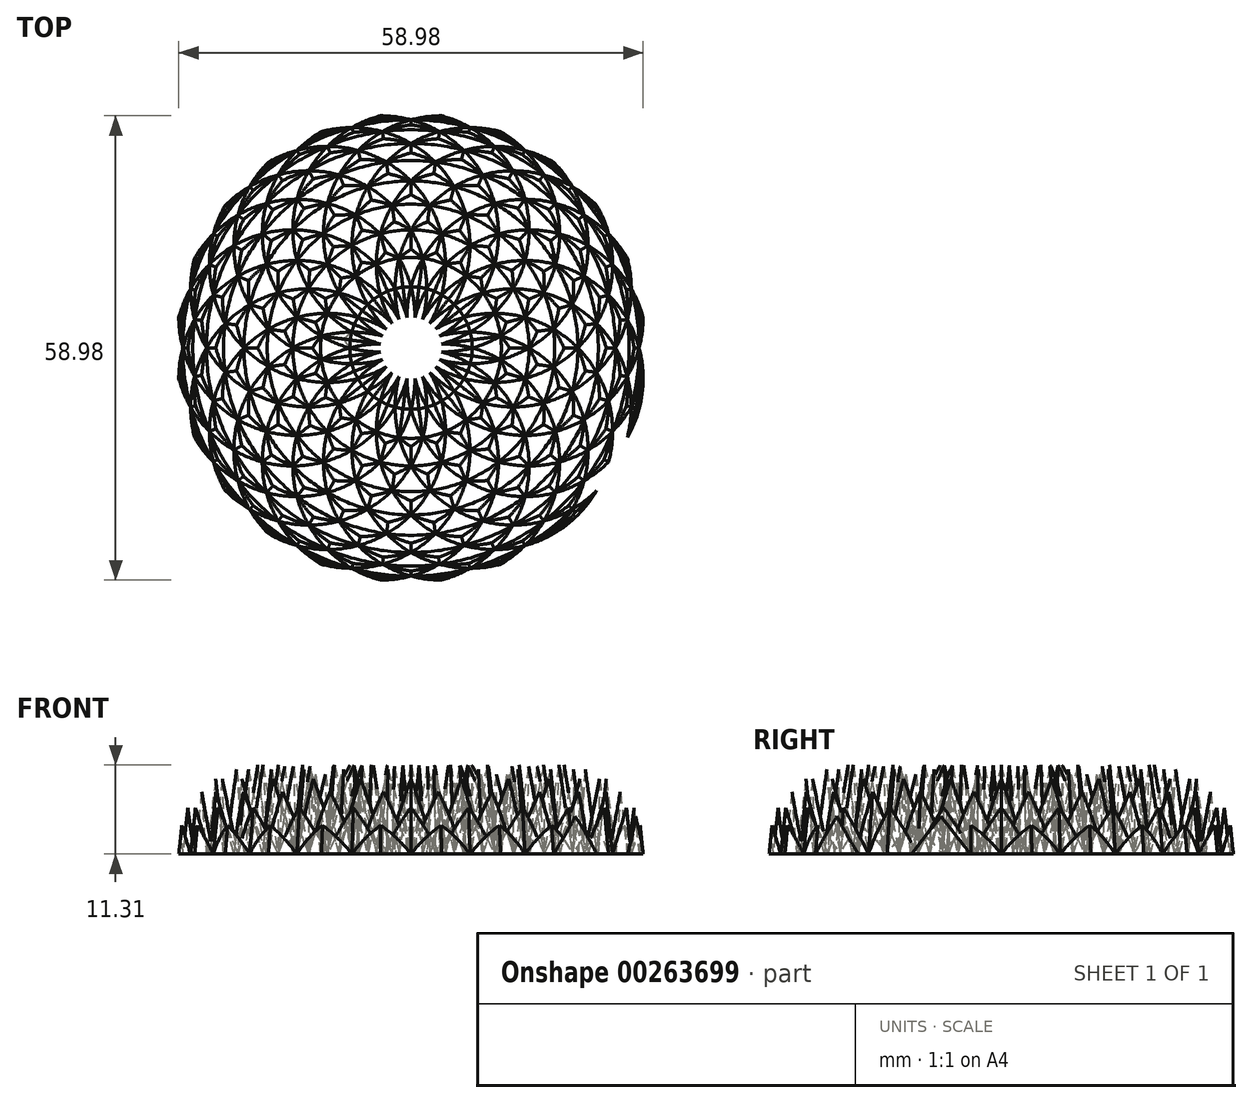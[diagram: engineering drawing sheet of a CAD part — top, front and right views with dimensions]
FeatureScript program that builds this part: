
annotation { "Feature Type Name" : "Feature", "Feature Type Description" : "" }
export const myFeature = defineFeature(function(context is Context, id is Id, definition is map)
    precondition{}
    {
        {
            var Q0;
            Q0=qCreatedBy(makeId("Top.planeOp"),FACE);
            var sketch = newSketch(context, id + "F0", { "sketchPlane" : qUnion([Q0])});
            skCircle(sketch, "E0", {"center": v(0, 0) * mm, "radius": 15 * mm});
            skLineSegment(sketch, "E1", {"start": v(-15, 0) * mm, "end": v(15, 0) * mm, "construction": true});
            skLineSegment(sketch, "E2", {"start": v(0, 15) * mm, "end": v(0, -15) * mm, "construction": true});
            skCircle(sketch, "E3", {"center": v(15, 0) * mm, "radius": 15 * mm});
            skCircle(sketch, "E4", {"center": v(7.5, 13) * mm, "radius": 15 * mm});
            skCircle(sketch, "E5", {"center": v(7.5, -13) * mm, "radius": 15 * mm});
            skCircle(sketch, "E6", {"center": v(-7.5, 13) * mm, "radius": 15 * mm});
            skCircle(sketch, "E7", {"center": v(-7.5, -13) * mm, "radius": 15 * mm});
            skCircle(sketch, "E8", {"center": v(-15, 0) * mm, "radius": 15 * mm});
            skLineSegment(sketch, "E9", {"start": v(0, 0) * mm, "end": v(22.5, 13) * mm, "construction": true});
            skCircle(sketch, "E10", {"center": v(13, 7.5) * mm, "radius": 15 * mm});
            skCircle(sketch, "E11", {"center": v(13, -7.5) * mm, "radius": 15 * mm});
            skCircle(sketch, "E12", {"center": v(0, -15) * mm, "radius": 15 * mm});
            skCircle(sketch, "E13", {"center": v(-13, -7.5) * mm, "radius": 15 * mm});
            skCircle(sketch, "E14", {"center": v(-13, 7.5) * mm, "radius": 15 * mm});
            skCircle(sketch, "E15", {"center": v(0, 15) * mm, "radius": 15 * mm});
            skLineSegment(sketch, "E16", {"start": v(7.5, 2) * mm, "end": v(20.5, 5.5) * mm, "construction": true});
            skCircle(sketch, "E17", {"center": v(14.49, 3.88) * mm, "radius": 15 * mm});
            skCircle(sketch, "E18", {"center": v(10.6, -10.6) * mm, "radius": 15 * mm});
            skCircle(sketch, "E19", {"center": v(-3.88, -14.49) * mm, "radius": 15 * mm});
            skCircle(sketch, "E20", {"center": v(-14.49, -3.88) * mm, "radius": 15 * mm});
            skCircle(sketch, "E21", {"center": v(-10.6, 10.6) * mm, "radius": 15 * mm});
            skCircle(sketch, "E22", {"center": v(3.88, 14.49) * mm, "radius": 15 * mm});
            skLineSegment(sketch, "E23", {"start": v(-2, 7.5) * mm, "end": v(-5.5, 20.5) * mm, "construction": true});
            skCircle(sketch, "E24", {"center": v(-3.88, 14.49) * mm, "radius": 15 * mm});
            skCircle(sketch, "E25", {"center": v(10.6, 10.6) * mm, "radius": 15 * mm});
            skCircle(sketch, "E26", {"center": v(14.49, -3.88) * mm, "radius": 15 * mm});
            skCircle(sketch, "E27", {"center": v(3.88, -14.49) * mm, "radius": 15 * mm});
            skCircle(sketch, "E28", {"center": v(-10.6, -10.6) * mm, "radius": 15 * mm});
            skCircle(sketch, "E29", {"center": v(-14.49, 3.88) * mm, "radius": 15 * mm});
            skCircle(sketch, "E30", {"center": v(0, 0) * mm, "radius": 18.26 * mm});
            skLineSegment(sketch, "E31", {"start": v(-6.99, 16.87) * mm, "end": v(-2.38, 18.1) * mm, "construction": true});
            skCircle(sketch, "E32", {"center": v(0, 0) * mm, "radius": 21.21 * mm});
            skLineSegment(sketch, "E33", {"start": v(0, 0) * mm, "end": v(7.5, 28) * mm, "construction": true});
            skCircle(sketch, "E34", {"center": v(0, 0) * mm, "radius": 28.98 * mm});
            skLineSegment(sketch, "E35", {"start": v(0, 0) * mm, "end": v(3.1, 23.6) * mm, "construction": true});
            skCircle(sketch, "E36", {"center": v(0, 0) * mm, "radius": 23.8 * mm});
            skLineSegment(sketch, "E37", {"start": v(0, 0) * mm, "end": v(-3.62, 27.48) * mm, "construction": true});
            skCircle(sketch, "E38", {"center": v(0, 0) * mm, "radius": 27.72 * mm});
            skLineSegment(sketch, "E39", {"start": v(0, 0) * mm, "end": v(-13, 22.5) * mm, "construction": true});
            skCircle(sketch, "E40", {"center": v(0, 0) * mm, "radius": 25.98 * mm});
            skLineSegment(sketch, "E41", {"start": v(0, 0) * mm, "end": v(-9.1, 6.99) * mm, "construction": true});
            skCircle(sketch, "E42", {"center": v(0, 0) * mm, "radius": 11.48 * mm});
            skLineSegment(sketch, "E43", {"start": v(0, 0) * mm, "end": v(-6.72, 3.88) * mm, "construction": true});
            skCircle(sketch, "E44", {"center": v(0, 0) * mm, "radius": 7.76 * mm});
            skLineSegment(sketch, "E45", {"start": v(0, 0) * mm, "end": v(-2.38, -3.1) * mm, "construction": true});
            skCircle(sketch, "E46", {"center": v(0, 0) * mm, "radius": 3.92 * mm});
            skCircle(sketch, "E47", {"center": v(0, 0) * mm, "radius": 30 * mm});
            skSolve(sketch);
        }
        {
            var Q0;
            {var subQ0=sQuery(id+"F0.wireOp",EDGE,"E44");var subQ1=sQuery(id+"F0.wireOp",EDGE,"E3");var subQ2=makeQuery(id+"F0.imprint","INTERSECT",VERTEX,{"derivedFrom":[subQ1,sQuery(id+"F0.wireOp",EDGE,"E14"),subQ0]});Q0=makeQuery(id+"F0.imprint","IMPRINT",FACE,{"disambiguationData":[TD([[makeQuery(id+"F0.imprint","IMPRINT",EDGE,{"disambiguationData":[TD([[subQ2,-1.0]])],"derivedFrom":subQ1}),-1.0]])]});}
            var Q1;
            {var subQ0=sQuery(id+"F0.wireOp",EDGE,"E44");var subQ1=sQuery(id+"F0.wireOp",EDGE,"E14");var subQ2=makeQuery(id+"F0.imprint","INTERSECT",VERTEX,{"derivedFrom":[sQuery(id+"F0.wireOp",EDGE,"E3"),subQ1,subQ0]});Q1=makeQuery(id+"F0.imprint","IMPRINT",FACE,{"disambiguationData":[TD([[makeQuery(id+"F0.imprint","IMPRINT",EDGE,{"disambiguationData":[TD([[subQ2,-1.0]])],"derivedFrom":subQ1}),1.0]])]});}
            var Q2;
            {var subQ0=sQuery(id+"F0.wireOp",EDGE,"E44");var subQ1=sQuery(id+"F0.wireOp",EDGE,"E14");var subQ2=makeQuery(id+"F0.imprint","INTERSECT",VERTEX,{"derivedFrom":[sQuery(id+"F0.wireOp",EDGE,"E3"),subQ1,subQ0]});Q2=makeQuery(id+"F0.imprint","IMPRINT",FACE,{"disambiguationData":[TD([[makeQuery(id+"F0.imprint","IMPRINT",EDGE,{"disambiguationData":[TD([[subQ2,1.0]])],"derivedFrom":subQ1}),-1.0]])]});}
            var Q3;
            {var subQ0=sQuery(id+"F0.wireOp",EDGE,"E21");var subQ1=sQuery(id+"F0.wireOp",EDGE,"E3");var subQ2=makeQuery(id+"F0.imprint","INTERSECT",VERTEX,{"derivedFrom":[subQ1,subQ0,sQuery(id+"F0.wireOp",EDGE,"E42")]});Q3=makeQuery(id+"F0.imprint","IMPRINT",FACE,{"disambiguationData":[TD([[makeQuery(id+"F0.imprint","IMPRINT",EDGE,{"disambiguationData":[TD([[subQ2,-1.0]])],"derivedFrom":subQ1}),1.0]])]});}
            var Q4;
            {var subQ0=sQuery(id+"F0.wireOp",EDGE,"E44");var subQ1=sQuery(id+"F0.wireOp",EDGE,"E11");var subQ2=makeQuery(id+"F0.imprint","INTERSECT",VERTEX,{"derivedFrom":[sQuery(id+"F0.wireOp",EDGE,"E6"),subQ1,subQ0]});Q4=makeQuery(id+"F0.imprint","IMPRINT",FACE,{"disambiguationData":[TD([[makeQuery(id+"F0.imprint","IMPRINT",EDGE,{"disambiguationData":[TD([[subQ2,-1.0]])],"derivedFrom":subQ1}),-1.0]])]});}
            var Q5;
            {var subQ0=sQuery(id+"F0.wireOp",EDGE,"E44");var subQ1=sQuery(id+"F0.wireOp",EDGE,"E6");var subQ2=makeQuery(id+"F0.imprint","INTERSECT",VERTEX,{"derivedFrom":[subQ1,sQuery(id+"F0.wireOp",EDGE,"E11"),subQ0]});Q5=makeQuery(id+"F0.imprint","IMPRINT",FACE,{"disambiguationData":[TD([[makeQuery(id+"F0.imprint","IMPRINT",EDGE,{"disambiguationData":[TD([[subQ2,-1.0]])],"derivedFrom":subQ1}),1.0]])]});}
            var Q6;
            {var subQ0=sQuery(id+"F0.wireOp",EDGE,"E18");var subQ1=sQuery(id+"F0.wireOp",EDGE,"E6");var subQ2=makeQuery(id+"F0.imprint","INTERSECT",VERTEX,{"derivedFrom":[subQ1,subQ0,sQuery(id+"F0.wireOp",EDGE,"E46")]});Q6=makeQuery(id+"F0.imprint","IMPRINT",FACE,{"disambiguationData":[TD([[makeQuery(id+"F0.imprint","IMPRINT",EDGE,{"disambiguationData":[TD([[subQ2,-1.0]])],"derivedFrom":subQ1}),-1.0]])]});}
            var Q7;
            {var subQ0=sQuery(id+"F0.wireOp",EDGE,"E44");var subQ1=sQuery(id+"F0.wireOp",EDGE,"E11");var subQ2=makeQuery(id+"F0.imprint","INTERSECT",VERTEX,{"derivedFrom":[sQuery(id+"F0.wireOp",EDGE,"E6"),subQ1,subQ0]});Q7=makeQuery(id+"F0.imprint","IMPRINT",FACE,{"disambiguationData":[TD([[makeQuery(id+"F0.imprint","IMPRINT",EDGE,{"disambiguationData":[TD([[subQ2,1.0]])],"derivedFrom":subQ1}),1.0]])]});}
            var Q8;
            {var subQ0=sQuery(id+"F0.wireOp",EDGE,"E44");var subQ1=sQuery(id+"F0.wireOp",EDGE,"E5");var subQ2=makeQuery(id+"F0.imprint","INTERSECT",VERTEX,{"derivedFrom":[subQ1,sQuery(id+"F0.wireOp",EDGE,"E15"),subQ0]});Q8=makeQuery(id+"F0.imprint","IMPRINT",FACE,{"disambiguationData":[TD([[makeQuery(id+"F0.imprint","IMPRINT",EDGE,{"disambiguationData":[TD([[subQ2,-1.0]])],"derivedFrom":subQ1}),-1.0]])]});}
            var Q9;
            {var subQ0=sQuery(id+"F0.wireOp",EDGE,"E44");var subQ1=sQuery(id+"F0.wireOp",EDGE,"E15");var subQ2=makeQuery(id+"F0.imprint","INTERSECT",VERTEX,{"derivedFrom":[sQuery(id+"F0.wireOp",EDGE,"E5"),subQ1,subQ0]});Q9=makeQuery(id+"F0.imprint","IMPRINT",FACE,{"disambiguationData":[TD([[makeQuery(id+"F0.imprint","IMPRINT",EDGE,{"disambiguationData":[TD([[subQ2,-1.0]])],"derivedFrom":subQ1}),1.0]])]});}
            var Q10;
            {var subQ0=sQuery(id+"F0.wireOp",EDGE,"E44");var subQ1=sQuery(id+"F0.wireOp",EDGE,"E15");var subQ2=makeQuery(id+"F0.imprint","INTERSECT",VERTEX,{"derivedFrom":[sQuery(id+"F0.wireOp",EDGE,"E5"),subQ1,subQ0]});Q10=makeQuery(id+"F0.imprint","IMPRINT",FACE,{"disambiguationData":[TD([[makeQuery(id+"F0.imprint","IMPRINT",EDGE,{"disambiguationData":[TD([[subQ2,1.0]])],"derivedFrom":subQ1}),-1.0]])]});}
            var Q11;
            {var subQ0=sQuery(id+"F0.wireOp",EDGE,"E22");var subQ1=sQuery(id+"F0.wireOp",EDGE,"E5");var subQ2=makeQuery(id+"F0.imprint","INTERSECT",VERTEX,{"derivedFrom":[subQ1,subQ0,sQuery(id+"F0.wireOp",EDGE,"E42")]});Q11=makeQuery(id+"F0.imprint","IMPRINT",FACE,{"disambiguationData":[TD([[makeQuery(id+"F0.imprint","IMPRINT",EDGE,{"disambiguationData":[TD([[subQ2,-1.0]])],"derivedFrom":subQ1}),1.0]])]});}
            var Q12;
            {var subQ0=sQuery(id+"F0.wireOp",EDGE,"E44");var subQ1=sQuery(id+"F0.wireOp",EDGE,"E12");var subQ2=makeQuery(id+"F0.imprint","INTERSECT",VERTEX,{"derivedFrom":[sQuery(id+"F0.wireOp",EDGE,"E4"),subQ1,subQ0]});Q12=makeQuery(id+"F0.imprint","IMPRINT",FACE,{"disambiguationData":[TD([[makeQuery(id+"F0.imprint","IMPRINT",EDGE,{"disambiguationData":[TD([[subQ2,-1.0]])],"derivedFrom":subQ1}),-1.0]])]});}
            var Q13;
            {var subQ0=sQuery(id+"F0.wireOp",EDGE,"E44");var subQ1=sQuery(id+"F0.wireOp",EDGE,"E4");var subQ2=makeQuery(id+"F0.imprint","INTERSECT",VERTEX,{"derivedFrom":[subQ1,sQuery(id+"F0.wireOp",EDGE,"E12"),subQ0]});Q13=makeQuery(id+"F0.imprint","IMPRINT",FACE,{"disambiguationData":[TD([[makeQuery(id+"F0.imprint","IMPRINT",EDGE,{"disambiguationData":[TD([[subQ2,-1.0]])],"derivedFrom":subQ1}),1.0]])]});}
            var Q14;
            {var subQ0=sQuery(id+"F0.wireOp",EDGE,"E19");var subQ1=sQuery(id+"F0.wireOp",EDGE,"E4");var subQ2=makeQuery(id+"F0.imprint","INTERSECT",VERTEX,{"derivedFrom":[subQ1,subQ0,sQuery(id+"F0.wireOp",EDGE,"E46")]});Q14=makeQuery(id+"F0.imprint","IMPRINT",FACE,{"disambiguationData":[TD([[makeQuery(id+"F0.imprint","IMPRINT",EDGE,{"disambiguationData":[TD([[subQ2,-1.0]])],"derivedFrom":subQ1}),-1.0]])]});}
            var Q15;
            {var subQ0=sQuery(id+"F0.wireOp",EDGE,"E44");var subQ1=sQuery(id+"F0.wireOp",EDGE,"E12");var subQ2=makeQuery(id+"F0.imprint","INTERSECT",VERTEX,{"derivedFrom":[sQuery(id+"F0.wireOp",EDGE,"E4"),subQ1,subQ0]});Q15=makeQuery(id+"F0.imprint","IMPRINT",FACE,{"disambiguationData":[TD([[makeQuery(id+"F0.imprint","IMPRINT",EDGE,{"disambiguationData":[TD([[subQ2,1.0]])],"derivedFrom":subQ1}),1.0]])]});}
            var Q16;
            {var subQ0=sQuery(id+"F0.wireOp",EDGE,"E44");var subQ1=sQuery(id+"F0.wireOp",EDGE,"E7");var subQ2=makeQuery(id+"F0.imprint","INTERSECT",VERTEX,{"derivedFrom":[subQ1,sQuery(id+"F0.wireOp",EDGE,"E10"),subQ0]});Q16=makeQuery(id+"F0.imprint","IMPRINT",FACE,{"disambiguationData":[TD([[makeQuery(id+"F0.imprint","IMPRINT",EDGE,{"disambiguationData":[TD([[subQ2,-1.0]])],"derivedFrom":subQ1}),-1.0]])]});}
            var Q17;
            {var subQ0=sQuery(id+"F0.wireOp",EDGE,"E44");var subQ1=sQuery(id+"F0.wireOp",EDGE,"E10");var subQ2=makeQuery(id+"F0.imprint","INTERSECT",VERTEX,{"derivedFrom":[sQuery(id+"F0.wireOp",EDGE,"E7"),subQ1,subQ0]});Q17=makeQuery(id+"F0.imprint","IMPRINT",FACE,{"disambiguationData":[TD([[makeQuery(id+"F0.imprint","IMPRINT",EDGE,{"disambiguationData":[TD([[subQ2,-1.0]])],"derivedFrom":subQ1}),1.0]])]});}
            var Q18;
            {var subQ0=sQuery(id+"F0.wireOp",EDGE,"E44");var subQ1=sQuery(id+"F0.wireOp",EDGE,"E10");var subQ2=makeQuery(id+"F0.imprint","INTERSECT",VERTEX,{"derivedFrom":[sQuery(id+"F0.wireOp",EDGE,"E7"),subQ1,subQ0]});Q18=makeQuery(id+"F0.imprint","IMPRINT",FACE,{"disambiguationData":[TD([[makeQuery(id+"F0.imprint","IMPRINT",EDGE,{"disambiguationData":[TD([[subQ2,1.0]])],"derivedFrom":subQ1}),-1.0]])]});}
            var Q19;
            {var subQ0=sQuery(id+"F0.wireOp",EDGE,"E17");var subQ1=sQuery(id+"F0.wireOp",EDGE,"E7");var subQ2=makeQuery(id+"F0.imprint","INTERSECT",VERTEX,{"derivedFrom":[subQ1,subQ0,sQuery(id+"F0.wireOp",EDGE,"E42")]});Q19=makeQuery(id+"F0.imprint","IMPRINT",FACE,{"disambiguationData":[TD([[makeQuery(id+"F0.imprint","IMPRINT",EDGE,{"disambiguationData":[TD([[subQ2,-1.0]])],"derivedFrom":subQ1}),1.0]])]});}
            var Q20;
            {var subQ0=sQuery(id+"F0.wireOp",EDGE,"E44");var subQ1=sQuery(id+"F0.wireOp",EDGE,"E13");var subQ2=makeQuery(id+"F0.imprint","INTERSECT",VERTEX,{"derivedFrom":[sQuery(id+"F0.wireOp",EDGE,"E3"),subQ1,subQ0]});Q20=makeQuery(id+"F0.imprint","IMPRINT",FACE,{"disambiguationData":[TD([[makeQuery(id+"F0.imprint","IMPRINT",EDGE,{"disambiguationData":[TD([[subQ2,-1.0]])],"derivedFrom":subQ1}),-1.0]])]});}
            var Q21;
            {var subQ0=sQuery(id+"F0.wireOp",EDGE,"E44");var subQ1=sQuery(id+"F0.wireOp",EDGE,"E3");var subQ2=makeQuery(id+"F0.imprint","INTERSECT",VERTEX,{"derivedFrom":[subQ1,sQuery(id+"F0.wireOp",EDGE,"E13"),subQ0]});Q21=makeQuery(id+"F0.imprint","IMPRINT",FACE,{"disambiguationData":[TD([[makeQuery(id+"F0.imprint","IMPRINT",EDGE,{"disambiguationData":[TD([[subQ2,-1.0]])],"derivedFrom":subQ1}),1.0]])]});}
            var Q22;
            {var subQ0=sQuery(id+"F0.wireOp",EDGE,"E20");var subQ1=sQuery(id+"F0.wireOp",EDGE,"E3");var subQ2=makeQuery(id+"F0.imprint","INTERSECT",VERTEX,{"derivedFrom":[subQ1,subQ0,sQuery(id+"F0.wireOp",EDGE,"E46")]});Q22=makeQuery(id+"F0.imprint","IMPRINT",FACE,{"disambiguationData":[TD([[makeQuery(id+"F0.imprint","IMPRINT",EDGE,{"disambiguationData":[TD([[subQ2,-1.0]])],"derivedFrom":subQ1}),-1.0]])]});}
            var Q23;
            {var subQ0=sQuery(id+"F0.wireOp",EDGE,"E44");var subQ1=sQuery(id+"F0.wireOp",EDGE,"E13");var subQ2=makeQuery(id+"F0.imprint","INTERSECT",VERTEX,{"derivedFrom":[sQuery(id+"F0.wireOp",EDGE,"E3"),subQ1,subQ0]});Q23=makeQuery(id+"F0.imprint","IMPRINT",FACE,{"disambiguationData":[TD([[makeQuery(id+"F0.imprint","IMPRINT",EDGE,{"disambiguationData":[TD([[subQ2,1.0]])],"derivedFrom":subQ1}),1.0]])]});}
            var Q24;
            {var subQ0=sQuery(id+"F0.wireOp",EDGE,"E44");var subQ1=sQuery(id+"F0.wireOp",EDGE,"E8");var subQ2=makeQuery(id+"F0.imprint","INTERSECT",VERTEX,{"derivedFrom":[subQ1,sQuery(id+"F0.wireOp",EDGE,"E11"),subQ0]});Q24=makeQuery(id+"F0.imprint","IMPRINT",FACE,{"disambiguationData":[TD([[makeQuery(id+"F0.imprint","IMPRINT",EDGE,{"disambiguationData":[TD([[subQ2,-1.0]])],"derivedFrom":subQ1}),-1.0]])]});}
            var Q25;
            {var subQ0=sQuery(id+"F0.wireOp",EDGE,"E44");var subQ1=sQuery(id+"F0.wireOp",EDGE,"E11");var subQ2=makeQuery(id+"F0.imprint","INTERSECT",VERTEX,{"derivedFrom":[sQuery(id+"F0.wireOp",EDGE,"E8"),subQ1,subQ0]});Q25=makeQuery(id+"F0.imprint","IMPRINT",FACE,{"disambiguationData":[TD([[makeQuery(id+"F0.imprint","IMPRINT",EDGE,{"disambiguationData":[TD([[subQ2,-1.0]])],"derivedFrom":subQ1}),1.0]])]});}
            var Q26;
            {var subQ0=sQuery(id+"F0.wireOp",EDGE,"E44");var subQ1=sQuery(id+"F0.wireOp",EDGE,"E11");var subQ2=makeQuery(id+"F0.imprint","INTERSECT",VERTEX,{"derivedFrom":[sQuery(id+"F0.wireOp",EDGE,"E8"),subQ1,subQ0]});Q26=makeQuery(id+"F0.imprint","IMPRINT",FACE,{"disambiguationData":[TD([[makeQuery(id+"F0.imprint","IMPRINT",EDGE,{"disambiguationData":[TD([[subQ2,1.0]])],"derivedFrom":subQ1}),-1.0]])]});}
            var Q27;
            {var subQ0=sQuery(id+"F0.wireOp",EDGE,"E18");var subQ1=sQuery(id+"F0.wireOp",EDGE,"E8");var subQ2=makeQuery(id+"F0.imprint","INTERSECT",VERTEX,{"derivedFrom":[subQ1,subQ0,sQuery(id+"F0.wireOp",EDGE,"E42")]});Q27=makeQuery(id+"F0.imprint","IMPRINT",FACE,{"disambiguationData":[TD([[makeQuery(id+"F0.imprint","IMPRINT",EDGE,{"disambiguationData":[TD([[subQ2,-1.0]])],"derivedFrom":subQ1}),1.0]])]});}
            var Q28;
            {var subQ0=sQuery(id+"F0.wireOp",EDGE,"E44");var subQ1=sQuery(id+"F0.wireOp",EDGE,"E14");var subQ2=makeQuery(id+"F0.imprint","INTERSECT",VERTEX,{"derivedFrom":[sQuery(id+"F0.wireOp",EDGE,"E5"),subQ1,subQ0]});Q28=makeQuery(id+"F0.imprint","IMPRINT",FACE,{"disambiguationData":[TD([[makeQuery(id+"F0.imprint","IMPRINT",EDGE,{"disambiguationData":[TD([[subQ2,-1.0]])],"derivedFrom":subQ1}),-1.0]])]});}
            var Q29;
            {var subQ0=sQuery(id+"F0.wireOp",EDGE,"E44");var subQ1=sQuery(id+"F0.wireOp",EDGE,"E5");var subQ2=makeQuery(id+"F0.imprint","INTERSECT",VERTEX,{"derivedFrom":[subQ1,sQuery(id+"F0.wireOp",EDGE,"E14"),subQ0]});Q29=makeQuery(id+"F0.imprint","IMPRINT",FACE,{"disambiguationData":[TD([[makeQuery(id+"F0.imprint","IMPRINT",EDGE,{"disambiguationData":[TD([[subQ2,-1.0]])],"derivedFrom":subQ1}),1.0]])]});}
            var Q30;
            {var subQ0=sQuery(id+"F0.wireOp",EDGE,"E21");var subQ1=sQuery(id+"F0.wireOp",EDGE,"E5");var subQ2=makeQuery(id+"F0.imprint","INTERSECT",VERTEX,{"derivedFrom":[subQ1,subQ0,sQuery(id+"F0.wireOp",EDGE,"E46")]});Q30=makeQuery(id+"F0.imprint","IMPRINT",FACE,{"disambiguationData":[TD([[makeQuery(id+"F0.imprint","IMPRINT",EDGE,{"disambiguationData":[TD([[subQ2,-1.0]])],"derivedFrom":subQ1}),-1.0]])]});}
            var Q31;
            {var subQ0=sQuery(id+"F0.wireOp",EDGE,"E44");var subQ1=sQuery(id+"F0.wireOp",EDGE,"E14");var subQ2=makeQuery(id+"F0.imprint","INTERSECT",VERTEX,{"derivedFrom":[sQuery(id+"F0.wireOp",EDGE,"E5"),subQ1,subQ0]});Q31=makeQuery(id+"F0.imprint","IMPRINT",FACE,{"disambiguationData":[TD([[makeQuery(id+"F0.imprint","IMPRINT",EDGE,{"disambiguationData":[TD([[subQ2,1.0]])],"derivedFrom":subQ1}),1.0]])]});}
            var Q32;
            {var subQ0=sQuery(id+"F0.wireOp",EDGE,"E44");var subQ1=sQuery(id+"F0.wireOp",EDGE,"E6");var subQ2=makeQuery(id+"F0.imprint","INTERSECT",VERTEX,{"derivedFrom":[subQ1,sQuery(id+"F0.wireOp",EDGE,"E12"),subQ0]});Q32=makeQuery(id+"F0.imprint","IMPRINT",FACE,{"disambiguationData":[TD([[makeQuery(id+"F0.imprint","IMPRINT",EDGE,{"disambiguationData":[TD([[subQ2,-1.0]])],"derivedFrom":subQ1}),-1.0]])]});}
            var Q33;
            {var subQ0=sQuery(id+"F0.wireOp",EDGE,"E44");var subQ1=sQuery(id+"F0.wireOp",EDGE,"E12");var subQ2=makeQuery(id+"F0.imprint","INTERSECT",VERTEX,{"derivedFrom":[sQuery(id+"F0.wireOp",EDGE,"E6"),subQ1,subQ0]});Q33=makeQuery(id+"F0.imprint","IMPRINT",FACE,{"disambiguationData":[TD([[makeQuery(id+"F0.imprint","IMPRINT",EDGE,{"disambiguationData":[TD([[subQ2,-1.0]])],"derivedFrom":subQ1}),1.0]])]});}
            var Q34;
            {var subQ0=sQuery(id+"F0.wireOp",EDGE,"E44");var subQ1=sQuery(id+"F0.wireOp",EDGE,"E12");var subQ2=makeQuery(id+"F0.imprint","INTERSECT",VERTEX,{"derivedFrom":[sQuery(id+"F0.wireOp",EDGE,"E6"),subQ1,subQ0]});Q34=makeQuery(id+"F0.imprint","IMPRINT",FACE,{"disambiguationData":[TD([[makeQuery(id+"F0.imprint","IMPRINT",EDGE,{"disambiguationData":[TD([[subQ2,1.0]])],"derivedFrom":subQ1}),-1.0]])]});}
            var Q35;
            {var subQ0=sQuery(id+"F0.wireOp",EDGE,"E19");var subQ1=sQuery(id+"F0.wireOp",EDGE,"E6");var subQ2=makeQuery(id+"F0.imprint","INTERSECT",VERTEX,{"derivedFrom":[subQ1,subQ0,sQuery(id+"F0.wireOp",EDGE,"E42")]});Q35=makeQuery(id+"F0.imprint","IMPRINT",FACE,{"disambiguationData":[TD([[makeQuery(id+"F0.imprint","IMPRINT",EDGE,{"disambiguationData":[TD([[subQ2,-1.0]])],"derivedFrom":subQ1}),1.0]])]});}
            var Q36;
            {var subQ0=sQuery(id+"F0.wireOp",EDGE,"E44");var subQ1=sQuery(id+"F0.wireOp",EDGE,"E15");var subQ2=makeQuery(id+"F0.imprint","INTERSECT",VERTEX,{"derivedFrom":[sQuery(id+"F0.wireOp",EDGE,"E7"),subQ1,subQ0]});Q36=makeQuery(id+"F0.imprint","IMPRINT",FACE,{"disambiguationData":[TD([[makeQuery(id+"F0.imprint","IMPRINT",EDGE,{"disambiguationData":[TD([[subQ2,-1.0]])],"derivedFrom":subQ1}),-1.0]])]});}
            var Q37;
            {var subQ0=sQuery(id+"F0.wireOp",EDGE,"E44");var subQ1=sQuery(id+"F0.wireOp",EDGE,"E7");var subQ2=makeQuery(id+"F0.imprint","INTERSECT",VERTEX,{"derivedFrom":[subQ1,sQuery(id+"F0.wireOp",EDGE,"E15"),subQ0]});Q37=makeQuery(id+"F0.imprint","IMPRINT",FACE,{"disambiguationData":[TD([[makeQuery(id+"F0.imprint","IMPRINT",EDGE,{"disambiguationData":[TD([[subQ2,-1.0]])],"derivedFrom":subQ1}),1.0]])]});}
            var Q38;
            {var subQ0=sQuery(id+"F0.wireOp",EDGE,"E22");var subQ1=sQuery(id+"F0.wireOp",EDGE,"E7");var subQ2=makeQuery(id+"F0.imprint","INTERSECT",VERTEX,{"derivedFrom":[subQ1,subQ0,sQuery(id+"F0.wireOp",EDGE,"E46")]});Q38=makeQuery(id+"F0.imprint","IMPRINT",FACE,{"disambiguationData":[TD([[makeQuery(id+"F0.imprint","IMPRINT",EDGE,{"disambiguationData":[TD([[subQ2,-1.0]])],"derivedFrom":subQ1}),-1.0]])]});}
            var Q39;
            {var subQ0=sQuery(id+"F0.wireOp",EDGE,"E44");var subQ1=sQuery(id+"F0.wireOp",EDGE,"E15");var subQ2=makeQuery(id+"F0.imprint","INTERSECT",VERTEX,{"derivedFrom":[sQuery(id+"F0.wireOp",EDGE,"E7"),subQ1,subQ0]});Q39=makeQuery(id+"F0.imprint","IMPRINT",FACE,{"disambiguationData":[TD([[makeQuery(id+"F0.imprint","IMPRINT",EDGE,{"disambiguationData":[TD([[subQ2,1.0]])],"derivedFrom":subQ1}),1.0]])]});}
            var Q40;
            {var subQ0=sQuery(id+"F0.wireOp",EDGE,"E44");var subQ1=sQuery(id+"F0.wireOp",EDGE,"E4");var subQ2=makeQuery(id+"F0.imprint","INTERSECT",VERTEX,{"derivedFrom":[subQ1,sQuery(id+"F0.wireOp",EDGE,"E13"),subQ0]});Q40=makeQuery(id+"F0.imprint","IMPRINT",FACE,{"disambiguationData":[TD([[makeQuery(id+"F0.imprint","IMPRINT",EDGE,{"disambiguationData":[TD([[subQ2,-1.0]])],"derivedFrom":subQ1}),-1.0]])]});}
            var Q41;
            {var subQ0=sQuery(id+"F0.wireOp",EDGE,"E44");var subQ1=sQuery(id+"F0.wireOp",EDGE,"E13");var subQ2=makeQuery(id+"F0.imprint","INTERSECT",VERTEX,{"derivedFrom":[sQuery(id+"F0.wireOp",EDGE,"E4"),subQ1,subQ0]});Q41=makeQuery(id+"F0.imprint","IMPRINT",FACE,{"disambiguationData":[TD([[makeQuery(id+"F0.imprint","IMPRINT",EDGE,{"disambiguationData":[TD([[subQ2,-1.0]])],"derivedFrom":subQ1}),1.0]])]});}
            var Q42;
            {var subQ0=sQuery(id+"F0.wireOp",EDGE,"E44");var subQ1=sQuery(id+"F0.wireOp",EDGE,"E13");var subQ2=makeQuery(id+"F0.imprint","INTERSECT",VERTEX,{"derivedFrom":[sQuery(id+"F0.wireOp",EDGE,"E4"),subQ1,subQ0]});Q42=makeQuery(id+"F0.imprint","IMPRINT",FACE,{"disambiguationData":[TD([[makeQuery(id+"F0.imprint","IMPRINT",EDGE,{"disambiguationData":[TD([[subQ2,1.0]])],"derivedFrom":subQ1}),-1.0]])]});}
            var Q43;
            {var subQ0=sQuery(id+"F0.wireOp",EDGE,"E20");var subQ1=sQuery(id+"F0.wireOp",EDGE,"E4");var subQ2=makeQuery(id+"F0.imprint","INTERSECT",VERTEX,{"derivedFrom":[subQ1,subQ0,sQuery(id+"F0.wireOp",EDGE,"E42")]});Q43=makeQuery(id+"F0.imprint","IMPRINT",FACE,{"disambiguationData":[TD([[makeQuery(id+"F0.imprint","IMPRINT",EDGE,{"disambiguationData":[TD([[subQ2,-1.0]])],"derivedFrom":subQ1}),1.0]])]});}
            var Q44;
            {var subQ0=sQuery(id+"F0.wireOp",EDGE,"E44");var subQ1=sQuery(id+"F0.wireOp",EDGE,"E10");var subQ2=makeQuery(id+"F0.imprint","INTERSECT",VERTEX,{"derivedFrom":[sQuery(id+"F0.wireOp",EDGE,"E8"),subQ1,subQ0]});Q44=makeQuery(id+"F0.imprint","IMPRINT",FACE,{"disambiguationData":[TD([[makeQuery(id+"F0.imprint","IMPRINT",EDGE,{"disambiguationData":[TD([[subQ2,-1.0]])],"derivedFrom":subQ1}),-1.0]])]});}
            var Q45;
            {var subQ0=sQuery(id+"F0.wireOp",EDGE,"E44");var subQ1=sQuery(id+"F0.wireOp",EDGE,"E8");var subQ2=makeQuery(id+"F0.imprint","INTERSECT",VERTEX,{"derivedFrom":[subQ1,sQuery(id+"F0.wireOp",EDGE,"E10"),subQ0]});Q45=makeQuery(id+"F0.imprint","IMPRINT",FACE,{"disambiguationData":[TD([[makeQuery(id+"F0.imprint","IMPRINT",EDGE,{"disambiguationData":[TD([[subQ2,-1.0]])],"derivedFrom":subQ1}),1.0]])]});}
            var Q46;
            {var subQ0=sQuery(id+"F0.wireOp",EDGE,"E17");var subQ1=sQuery(id+"F0.wireOp",EDGE,"E8");var subQ2=makeQuery(id+"F0.imprint","INTERSECT",VERTEX,{"derivedFrom":[subQ1,subQ0,sQuery(id+"F0.wireOp",EDGE,"E46")]});Q46=makeQuery(id+"F0.imprint","IMPRINT",FACE,{"disambiguationData":[TD([[makeQuery(id+"F0.imprint","IMPRINT",EDGE,{"disambiguationData":[TD([[subQ2,-1.0]])],"derivedFrom":subQ1}),-1.0]])]});}
            var Q47;
            {var subQ0=sQuery(id+"F0.wireOp",EDGE,"E44");var subQ1=sQuery(id+"F0.wireOp",EDGE,"E10");var subQ2=makeQuery(id+"F0.imprint","INTERSECT",VERTEX,{"derivedFrom":[sQuery(id+"F0.wireOp",EDGE,"E8"),subQ1,subQ0]});Q47=makeQuery(id+"F0.imprint","IMPRINT",FACE,{"disambiguationData":[TD([[makeQuery(id+"F0.imprint","IMPRINT",EDGE,{"disambiguationData":[TD([[subQ2,1.0]])],"derivedFrom":subQ1}),1.0]])]});}
            extrude(context, id + "F1", {"entities" : qUnion([Q0, Q1, Q2, Q3, Q4, Q5, Q6, Q7, Q8, Q9, Q10, Q11, Q12, Q13, Q14, Q15, Q16, Q17, Q18, Q19, Q20, Q21, Q22, Q23, Q24, Q25, Q26, Q27, Q28, Q29, Q30, Q31, Q32, Q33, Q34, Q35, Q36, Q37, Q38, Q39, Q40, Q41, Q42, Q43, Q44, Q45, Q46, Q47]), "depth" : 12 * mm, "hasDraft" : true, "draftAngle" : 5 * degree, "draftPullDirection" : true});
        }
        {
            var Q0;
            Q0=qCreatedBy(makeId("Top.planeOp"),FACE);
            var sketch = newSketch(context, id + "F2", { "sketchPlane" : qUnion([Q0])});
            skCircle(sketch, "E48.0", {"center": v(0, 0) * mm, "radius": 18.26 * mm});
            skCircle(sketch, "E48.1", {"center": v(0, 0) * mm, "radius": 3.92 * mm});
            skCircle(sketch, "E48.2", {"center": v(-14.49, 3.88) * mm, "radius": 15 * mm});
            skCircle(sketch, "E48.3", {"center": v(-10.6, -10.6) * mm, "radius": 15 * mm});
            skCircle(sketch, "E48.4", {"center": v(0, 0) * mm, "radius": 7.76 * mm});
            skCircle(sketch, "E48.5", {"center": v(0, 15) * mm, "radius": 15 * mm});
            skCircle(sketch, "E48.6", {"center": v(0, 0) * mm, "radius": 30 * mm});
            skLineSegment(sketch, "E48.7", {"start": v(-6.99, 16.87) * mm, "end": v(-2.38, 18.1) * mm});
            skCircle(sketch, "E48.9", {"center": v(0, 0) * mm, "radius": 21.21 * mm});
            skCircle(sketch, "E48.10", {"center": v(14.49, 3.88) * mm, "radius": 15 * mm});
            skCircle(sketch, "E48.12", {"center": v(10.6, -10.6) * mm, "radius": 15 * mm});
            skCircle(sketch, "E48.13", {"center": v(0, 0) * mm, "radius": 28.98 * mm});
            skCircle(sketch, "E48.14", {"center": v(-3.88, -14.49) * mm, "radius": 15 * mm});
            skLineSegment(sketch, "E48.15", {"start": v(0, 0) * mm, "end": v(3.1, 23.6) * mm});
            skCircle(sketch, "E48.16", {"center": v(-14.49, -3.88) * mm, "radius": 15 * mm});
            skCircle(sketch, "E48.17", {"center": v(0, 0) * mm, "radius": 23.8 * mm});
            skCircle(sketch, "E48.18", {"center": v(-10.6, 10.6) * mm, "radius": 15 * mm});
            skLineSegment(sketch, "E48.19", {"start": v(0, 0) * mm, "end": v(-3.62, 27.48) * mm});
            skCircle(sketch, "E48.20", {"center": v(0, 0) * mm, "radius": 27.72 * mm});
            skCircle(sketch, "E48.21", {"center": v(3.88, 14.49) * mm, "radius": 15 * mm});
            skCircle(sketch, "E48.24", {"center": v(0, 0) * mm, "radius": 25.98 * mm});
            skCircle(sketch, "E48.25", {"center": v(-3.88, 14.49) * mm, "radius": 15 * mm});
            skLineSegment(sketch, "E48.26", {"start": v(0, 0) * mm, "end": v(-9.1, 6.99) * mm});
            skCircle(sketch, "E48.27", {"center": v(10.6, 10.6) * mm, "radius": 15 * mm});
            skCircle(sketch, "E48.28", {"center": v(0, 0) * mm, "radius": 11.48 * mm});
            skCircle(sketch, "E48.29", {"center": v(14.49, -3.88) * mm, "radius": 15 * mm});
            skLineSegment(sketch, "E48.30", {"start": v(0, 0) * mm, "end": v(-6.72, 3.88) * mm});
            skCircle(sketch, "E48.31", {"center": v(3.88, -14.49) * mm, "radius": 15 * mm});
            skCircle(sketch, "E48.32", {"center": v(0, -15) * mm, "radius": 15 * mm});
            skCircle(sketch, "E48.33", {"center": v(-13, -7.5) * mm, "radius": 15 * mm});
            skCircle(sketch, "E48.34", {"center": v(-13, 7.5) * mm, "radius": 15 * mm});
            skCircle(sketch, "E48.35", {"center": v(0, 0) * mm, "radius": 15 * mm});
            skCircle(sketch, "E48.38", {"center": v(15, 0) * mm, "radius": 15 * mm});
            skCircle(sketch, "E48.39", {"center": v(7.5, 13) * mm, "radius": 15 * mm});
            skCircle(sketch, "E48.40", {"center": v(7.5, -13) * mm, "radius": 15 * mm});
            skCircle(sketch, "E48.41", {"center": v(-7.5, 13) * mm, "radius": 15 * mm});
            skCircle(sketch, "E48.42", {"center": v(-7.5, -13) * mm, "radius": 15 * mm});
            skCircle(sketch, "E48.43", {"center": v(-15, 0) * mm, "radius": 15 * mm});
            skCircle(sketch, "E48.45", {"center": v(13, 7.5) * mm, "radius": 15 * mm});
            skCircle(sketch, "E48.46", {"center": v(13, -7.5) * mm, "radius": 15 * mm});
            skCircle(sketch, "E48.47", {"center": v(13, -7.5) * mm, "radius": 15 * mm});
            skSolve(sketch);
        }
        {
            var Q0;
            {var subQ0=sQuery(id+"F2.wireOp",EDGE,"E48.28");var subQ1=sQuery(id+"F2.wireOp",EDGE,"E48.25");var subQ2=makeQuery(id+"F2.imprint","INTERSECT",VERTEX,{"derivedFrom":[subQ1,subQ0,sQuery(id+"F2.wireOp",EDGE,"E48.47")]});Q0=makeQuery(id+"F2.imprint","IMPRINT",FACE,{"disambiguationData":[TD([[makeQuery(id+"F2.imprint","IMPRINT",EDGE,{"disambiguationData":[TD([[subQ2,-1.0]])],"derivedFrom":subQ1}),1.0]])]});}
            var Q1;
            {var subQ0=sQuery(id+"F2.wireOp",EDGE,"E48.38");var subQ1=sQuery(id+"F2.wireOp",EDGE,"E48.28");var subQ2=makeQuery(id+"F2.imprint","INTERSECT",VERTEX,{"derivedFrom":[sQuery(id+"F2.wireOp",EDGE,"E48.18"),subQ1,subQ0]});Q1=makeQuery(id+"F2.imprint","IMPRINT",FACE,{"disambiguationData":[TD([[makeQuery(id+"F2.imprint","IMPRINT",EDGE,{"disambiguationData":[TD([[subQ2,1.0]])],"derivedFrom":subQ1}),-1.0]])]});}
            var Q2;
            {var subQ0=sQuery(id+"F2.wireOp",EDGE,"E48.18");var subQ1=sQuery(id+"F2.wireOp",EDGE,"E48.10");var subQ2=makeQuery(id+"F2.imprint","INTERSECT",VERTEX,{"derivedFrom":[subQ1,subQ0,sQuery(id+"F2.wireOp",EDGE,"E48.35")]});Q2=makeQuery(id+"F2.imprint","IMPRINT",FACE,{"disambiguationData":[TD([[makeQuery(id+"F2.imprint","IMPRINT",EDGE,{"disambiguationData":[TD([[subQ2,1.0]])],"derivedFrom":subQ0}),1.0]])]});}
            var Q3;
            {var subQ0=sQuery(id+"F2.wireOp",EDGE,"E48.45");var subQ3=sQuery(id+"F2.wireOp",EDGE,"E48.34");var subQ5=makeQuery(id+"F2.imprint","INTERSECT",VERTEX,{"derivedFrom":[subQ3,sQuery(id+"F2.wireOp",EDGE,"E48.35"),subQ0]});Q3=makeQuery(id+"F2.imprint","IMPRINT",FACE,{"disambiguationData":[TD([[makeQuery(id+"F2.imprint","IMPRINT",EDGE,{"disambiguationData":[TD([[subQ5,1.0]])],"derivedFrom":subQ3}),1.0]])]});}
            var Q4;
            {var subQ0=sQuery(id+"F2.wireOp",EDGE,"E48.27");var subQ1=sQuery(id+"F2.wireOp",EDGE,"E48.2");var subQ2=makeQuery(id+"F2.imprint","INTERSECT",VERTEX,{"derivedFrom":[subQ1,subQ0,sQuery(id+"F2.wireOp",EDGE,"E48.35")]});Q4=makeQuery(id+"F2.imprint","IMPRINT",FACE,{"disambiguationData":[TD([[makeQuery(id+"F2.imprint","IMPRINT",EDGE,{"disambiguationData":[TD([[subQ2,-1.0]])],"derivedFrom":subQ0}),1.0]])]});}
            var Q5;
            {var subQ0=sQuery(id+"F2.wireOp",EDGE,"E48.39");var subQ1=sQuery(id+"F2.wireOp",EDGE,"E48.28");var subQ2=makeQuery(id+"F2.imprint","INTERSECT",VERTEX,{"derivedFrom":[sQuery(id+"F2.wireOp",EDGE,"E48.16"),subQ1,subQ0]});Q5=makeQuery(id+"F2.imprint","IMPRINT",FACE,{"disambiguationData":[TD([[makeQuery(id+"F2.imprint","IMPRINT",EDGE,{"disambiguationData":[TD([[subQ2,1.0]])],"derivedFrom":subQ1}),-1.0]])]});}
            var Q6;
            {var subQ0=sQuery(id+"F2.wireOp",EDGE,"E48.28");var subQ1=sQuery(id+"F2.wireOp",EDGE,"E48.16");var subQ2=makeQuery(id+"F2.imprint","INTERSECT",VERTEX,{"derivedFrom":[subQ1,subQ0,sQuery(id+"F2.wireOp",EDGE,"E48.39")]});Q6=makeQuery(id+"F2.imprint","IMPRINT",FACE,{"disambiguationData":[TD([[makeQuery(id+"F2.imprint","IMPRINT",EDGE,{"disambiguationData":[TD([[subQ2,-1.0]])],"derivedFrom":subQ1}),1.0]])]});}
            var Q7;
            {var subQ0=sQuery(id+"F2.wireOp",EDGE,"E48.28");var subQ1=sQuery(id+"F2.wireOp",EDGE,"E48.5");var subQ2=makeQuery(id+"F2.imprint","INTERSECT",VERTEX,{"derivedFrom":[sQuery(id+"F2.wireOp",EDGE,"E48.3"),subQ1,subQ0]});Q7=makeQuery(id+"F2.imprint","IMPRINT",FACE,{"disambiguationData":[TD([[makeQuery(id+"F2.imprint","IMPRINT",EDGE,{"disambiguationData":[TD([[subQ2,1.0]])],"derivedFrom":subQ1}),1.0]])]});}
            var Q8;
            {var subQ0=sQuery(id+"F2.wireOp",EDGE,"E48.28");var subQ1=sQuery(id+"F2.wireOp",EDGE,"E48.3");var subQ2=makeQuery(id+"F2.imprint","INTERSECT",VERTEX,{"derivedFrom":[subQ1,sQuery(id+"F2.wireOp",EDGE,"E48.5"),subQ0]});Q8=makeQuery(id+"F2.imprint","IMPRINT",FACE,{"disambiguationData":[TD([[makeQuery(id+"F2.imprint","IMPRINT",EDGE,{"disambiguationData":[TD([[subQ2,-1.0]])],"derivedFrom":subQ1}),1.0]])]});}
            var Q9;
            {var subQ0=sQuery(id+"F2.wireOp",EDGE,"E48.41");var subQ1=sQuery(id+"F2.wireOp",EDGE,"E48.28");var subQ2=makeQuery(id+"F2.imprint","INTERSECT",VERTEX,{"derivedFrom":[sQuery(id+"F2.wireOp",EDGE,"E48.14"),subQ1,subQ0]});Q9=makeQuery(id+"F2.imprint","IMPRINT",FACE,{"disambiguationData":[TD([[makeQuery(id+"F2.imprint","IMPRINT",EDGE,{"disambiguationData":[TD([[subQ2,1.0]])],"derivedFrom":subQ1}),-1.0]])]});}
            var Q10;
            {var subQ0=sQuery(id+"F2.wireOp",EDGE,"E48.28");var subQ1=sQuery(id+"F2.wireOp",EDGE,"E48.14");var subQ2=makeQuery(id+"F2.imprint","INTERSECT",VERTEX,{"derivedFrom":[subQ1,subQ0,sQuery(id+"F2.wireOp",EDGE,"E48.41")]});Q10=makeQuery(id+"F2.imprint","IMPRINT",FACE,{"disambiguationData":[TD([[makeQuery(id+"F2.imprint","IMPRINT",EDGE,{"disambiguationData":[TD([[subQ2,-1.0]])],"derivedFrom":subQ1}),1.0]])]});}
            var Q11;
            {var subQ0=sQuery(id+"F2.wireOp",EDGE,"E48.32");var subQ1=sQuery(id+"F2.wireOp",EDGE,"E48.28");var subQ2=makeQuery(id+"F2.imprint","INTERSECT",VERTEX,{"derivedFrom":[sQuery(id+"F2.wireOp",EDGE,"E48.18"),subQ1,subQ0]});Q11=makeQuery(id+"F2.imprint","IMPRINT",FACE,{"disambiguationData":[TD([[makeQuery(id+"F2.imprint","IMPRINT",EDGE,{"disambiguationData":[TD([[subQ2,-1.0]])],"derivedFrom":subQ1}),-1.0]])]});}
            var Q12;
            {var subQ0=sQuery(id+"F2.wireOp",EDGE,"E48.31");var subQ1=sQuery(id+"F2.wireOp",EDGE,"E48.2");var subQ2=makeQuery(id+"F2.imprint","INTERSECT",VERTEX,{"derivedFrom":[subQ1,subQ0,sQuery(id+"F2.wireOp",EDGE,"E48.35")]});Q12=makeQuery(id+"F2.imprint","IMPRINT",FACE,{"disambiguationData":[TD([[makeQuery(id+"F2.imprint","IMPRINT",EDGE,{"disambiguationData":[TD([[subQ2,-1.0]])],"derivedFrom":subQ1}),1.0]])]});}
            var Q13;
            {var subQ0=sQuery(id+"F2.wireOp",EDGE,"E48.40");var subQ1=sQuery(id+"F2.wireOp",EDGE,"E48.28");var subQ2=makeQuery(id+"F2.imprint","INTERSECT",VERTEX,{"derivedFrom":[sQuery(id+"F2.wireOp",EDGE,"E48.2"),subQ1,subQ0]});Q13=makeQuery(id+"F2.imprint","IMPRINT",FACE,{"disambiguationData":[TD([[makeQuery(id+"F2.imprint","IMPRINT",EDGE,{"disambiguationData":[TD([[subQ2,-1.0]])],"derivedFrom":subQ1}),-1.0]])]});}
            var Q14;
            {var subQ0=sQuery(id+"F2.wireOp",EDGE,"E48.28");var subQ1=sQuery(id+"F2.wireOp",EDGE,"E48.12");var subQ2=makeQuery(id+"F2.imprint","INTERSECT",VERTEX,{"derivedFrom":[subQ1,subQ0,sQuery(id+"F2.wireOp",EDGE,"E48.43")]});Q14=makeQuery(id+"F2.imprint","IMPRINT",FACE,{"disambiguationData":[TD([[makeQuery(id+"F2.imprint","IMPRINT",EDGE,{"disambiguationData":[TD([[subQ2,-1.0]])],"derivedFrom":subQ1}),1.0]])]});}
            var Q15;
            {var subQ0=sQuery(id+"F2.wireOp",EDGE,"E48.47");var subQ1=sQuery(id+"F2.wireOp",EDGE,"E48.28");var subQ2=makeQuery(id+"F2.imprint","INTERSECT",VERTEX,{"derivedFrom":[sQuery(id+"F2.wireOp",EDGE,"E48.16"),subQ1,subQ0]});Q15=makeQuery(id+"F2.imprint","IMPRINT",FACE,{"disambiguationData":[TD([[makeQuery(id+"F2.imprint","IMPRINT",EDGE,{"disambiguationData":[TD([[subQ2,-1.0]])],"derivedFrom":subQ1}),-1.0]])]});}
            var Q16;
            {var subQ0=sQuery(id+"F2.wireOp",EDGE,"E48.28");var subQ1=sQuery(id+"F2.wireOp",EDGE,"E48.3");var subQ2=makeQuery(id+"F2.imprint","INTERSECT",VERTEX,{"derivedFrom":[subQ1,subQ0,sQuery(id+"F2.wireOp",EDGE,"E48.38")]});Q16=makeQuery(id+"F2.imprint","IMPRINT",FACE,{"disambiguationData":[TD([[makeQuery(id+"F2.imprint","IMPRINT",EDGE,{"disambiguationData":[TD([[subQ2,1.0]])],"derivedFrom":subQ1}),1.0]])]});}
            var Q17;
            {var subQ0=sQuery(id+"F2.wireOp",EDGE,"E48.38");var subQ1=sQuery(id+"F2.wireOp",EDGE,"E48.28");var subQ2=makeQuery(id+"F2.imprint","INTERSECT",VERTEX,{"derivedFrom":[sQuery(id+"F2.wireOp",EDGE,"E48.3"),subQ1,subQ0]});Q17=makeQuery(id+"F2.imprint","IMPRINT",FACE,{"disambiguationData":[TD([[makeQuery(id+"F2.imprint","IMPRINT",EDGE,{"disambiguationData":[TD([[subQ2,-1.0]])],"derivedFrom":subQ1}),-1.0]])]});}
            var Q18;
            {var subQ0=sQuery(id+"F2.wireOp",EDGE,"E48.28");var subQ1=sQuery(id+"F2.wireOp",EDGE,"E48.10");var subQ2=makeQuery(id+"F2.imprint","INTERSECT",VERTEX,{"derivedFrom":[subQ1,subQ0,sQuery(id+"F2.wireOp",EDGE,"E48.42")]});Q18=makeQuery(id+"F2.imprint","IMPRINT",FACE,{"disambiguationData":[TD([[makeQuery(id+"F2.imprint","IMPRINT",EDGE,{"disambiguationData":[TD([[subQ2,-1.0]])],"derivedFrom":subQ1}),1.0]])]});}
            var Q19;
            {var subQ0=sQuery(id+"F2.wireOp",EDGE,"E48.45");var subQ1=sQuery(id+"F2.wireOp",EDGE,"E48.28");var subQ2=makeQuery(id+"F2.imprint","INTERSECT",VERTEX,{"derivedFrom":[sQuery(id+"F2.wireOp",EDGE,"E48.14"),subQ1,subQ0]});Q19=makeQuery(id+"F2.imprint","IMPRINT",FACE,{"disambiguationData":[TD([[makeQuery(id+"F2.imprint","IMPRINT",EDGE,{"disambiguationData":[TD([[subQ2,-1.0]])],"derivedFrom":subQ1}),-1.0]])]});}
            var Q20;
            {var subQ0=sQuery(id+"F2.wireOp",EDGE,"E48.28");var subQ1=sQuery(id+"F2.wireOp",EDGE,"E48.27");var subQ2=makeQuery(id+"F2.imprint","INTERSECT",VERTEX,{"derivedFrom":[subQ1,subQ0,sQuery(id+"F2.wireOp",EDGE,"E48.32")]});Q20=makeQuery(id+"F2.imprint","IMPRINT",FACE,{"disambiguationData":[TD([[makeQuery(id+"F2.imprint","IMPRINT",EDGE,{"disambiguationData":[TD([[subQ2,-1.0]])],"derivedFrom":subQ1}),1.0]])]});}
            var Q21;
            {var subQ0=sQuery(id+"F2.wireOp",EDGE,"E48.40");var subQ1=sQuery(id+"F2.wireOp",EDGE,"E48.28");var subQ2=makeQuery(id+"F2.imprint","INTERSECT",VERTEX,{"derivedFrom":[sQuery(id+"F2.wireOp",EDGE,"E48.21"),subQ1,subQ0]});Q21=makeQuery(id+"F2.imprint","IMPRINT",FACE,{"disambiguationData":[TD([[makeQuery(id+"F2.imprint","IMPRINT",EDGE,{"disambiguationData":[TD([[subQ2,1.0]])],"derivedFrom":subQ1}),-1.0]])]});}
            var Q22;
            {var subQ0=sQuery(id+"F2.wireOp",EDGE,"E48.28");var subQ1=sQuery(id+"F2.wireOp",EDGE,"E48.12");var subQ2=makeQuery(id+"F2.imprint","INTERSECT",VERTEX,{"derivedFrom":[sQuery(id+"F2.wireOp",EDGE,"E48.5"),subQ1,subQ0]});Q22=makeQuery(id+"F2.imprint","IMPRINT",FACE,{"disambiguationData":[TD([[makeQuery(id+"F2.imprint","IMPRINT",EDGE,{"disambiguationData":[TD([[subQ2,1.0]])],"derivedFrom":subQ1}),1.0]])]});}
            var Q23;
            {var subQ0=sQuery(id+"F2.wireOp",EDGE,"E48.28");var subQ1=sQuery(id+"F2.wireOp",EDGE,"E48.5");var subQ2=makeQuery(id+"F2.imprint","INTERSECT",VERTEX,{"derivedFrom":[subQ1,sQuery(id+"F2.wireOp",EDGE,"E48.12"),subQ0]});Q23=makeQuery(id+"F2.imprint","IMPRINT",FACE,{"disambiguationData":[TD([[makeQuery(id+"F2.imprint","IMPRINT",EDGE,{"disambiguationData":[TD([[subQ2,-1.0]])],"derivedFrom":subQ1}),1.0]])]});}
            extrude(context, id + "F3", {"entities" : qUnion([Q0, Q1, Q2, Q3, Q4, Q5, Q6, Q7, Q8, Q9, Q10, Q11, Q12, Q13, Q14, Q15, Q16, Q17, Q18, Q19, Q20, Q21, Q22, Q23]), "depth" : 12 * mm, "hasDraft" : true, "draftAngle" : 6 * degree, "draftPullDirection" : true});
        }
        {
            var Q0;
            {var subQ0=sQuery(id+"F0.wireOp",EDGE,"E21");var subQ1=sQuery(id+"F0.wireOp",EDGE,"E0");var subQ2=makeQuery(id+"F0.imprint","INTERSECT",VERTEX,{"derivedFrom":[subQ1,sQuery(id+"F0.wireOp",EDGE,"E17"),subQ0]});Q0=makeQuery(id+"F0.imprint","IMPRINT",FACE,{"disambiguationData":[TD([[makeQuery(id+"F0.imprint","IMPRINT",EDGE,{"disambiguationData":[TD([[subQ2,-1.0]])],"derivedFrom":subQ1}),-1.0]])]});}
            var Q1;
            {var subQ0=sQuery(id+"F2.wireOp",EDGE,"E48.41");var subQ1=sQuery(id+"F2.wireOp",EDGE,"E48.10");var subQ2=makeQuery(id+"F2.imprint","INTERSECT",VERTEX,{"derivedFrom":[sQuery(id+"F2.wireOp",EDGE,"E48.0"),subQ1,subQ0]});Q1=makeQuery(id+"F2.imprint","IMPRINT",FACE,{"disambiguationData":[TD([[makeQuery(id+"F2.imprint","IMPRINT",EDGE,{"disambiguationData":[TD([[subQ2,-1.0]])],"derivedFrom":subQ1}),1.0]])]});}
            var Q2;
            {var subQ0=sQuery(id+"F2.wireOp",EDGE,"E48.38");var subQ1=sQuery(id+"F2.wireOp",EDGE,"E48.25");var subQ2=makeQuery(id+"F2.imprint","INTERSECT",VERTEX,{"derivedFrom":[sQuery(id+"F2.wireOp",EDGE,"E48.0"),subQ1,subQ0]});Q2=makeQuery(id+"F2.imprint","IMPRINT",FACE,{"disambiguationData":[TD([[makeQuery(id+"F2.imprint","IMPRINT",EDGE,{"disambiguationData":[TD([[subQ2,1.0]])],"derivedFrom":subQ1}),1.0]])]});}
            var Q3;
            {var subQ0=sQuery(id+"F0.wireOp",EDGE,"E15");var subQ1=sQuery(id+"F0.wireOp",EDGE,"E0");var subQ2=makeQuery(id+"F0.imprint","INTERSECT",VERTEX,{"derivedFrom":[subQ1,sQuery(id+"F0.wireOp",EDGE,"E11"),subQ0]});Q3=makeQuery(id+"F0.imprint","IMPRINT",FACE,{"disambiguationData":[TD([[makeQuery(id+"F0.imprint","IMPRINT",EDGE,{"disambiguationData":[TD([[subQ2,-1.0]])],"derivedFrom":subQ1}),-1.0]])]});}
            var Q4;
            {var subQ0=sQuery(id+"F2.wireOp",EDGE,"E48.47");var subQ1=sQuery(id+"F2.wireOp",EDGE,"E48.21");var subQ2=makeQuery(id+"F2.imprint","INTERSECT",VERTEX,{"derivedFrom":[sQuery(id+"F2.wireOp",EDGE,"E48.0"),subQ1,subQ0]});Q4=makeQuery(id+"F2.imprint","IMPRINT",FACE,{"disambiguationData":[TD([[makeQuery(id+"F2.imprint","IMPRINT",EDGE,{"disambiguationData":[TD([[subQ2,1.0]])],"derivedFrom":subQ1}),1.0]])]});}
            var Q5;
            {var subQ0=sQuery(id+"F2.wireOp",EDGE,"E48.39");var subQ1=sQuery(id+"F2.wireOp",EDGE,"E48.12");var subQ2=makeQuery(id+"F2.imprint","INTERSECT",VERTEX,{"derivedFrom":[sQuery(id+"F2.wireOp",EDGE,"E48.0"),subQ1,subQ0]});Q5=makeQuery(id+"F2.imprint","IMPRINT",FACE,{"disambiguationData":[TD([[makeQuery(id+"F2.imprint","IMPRINT",EDGE,{"disambiguationData":[TD([[subQ2,-1.0]])],"derivedFrom":subQ1}),1.0]])]});}
            var Q6;
            {var subQ0=sQuery(id+"F2.wireOp",EDGE,"E48.40");var subQ1=sQuery(id+"F2.wireOp",EDGE,"E48.27");var subQ2=makeQuery(id+"F2.imprint","INTERSECT",VERTEX,{"derivedFrom":[sQuery(id+"F2.wireOp",EDGE,"E48.0"),subQ1,subQ0]});Q6=makeQuery(id+"F2.imprint","IMPRINT",FACE,{"disambiguationData":[TD([[makeQuery(id+"F2.imprint","IMPRINT",EDGE,{"disambiguationData":[TD([[subQ2,1.0]])],"derivedFrom":subQ1}),1.0]])]});}
            var Q7;
            {var subQ0=sQuery(id+"F2.wireOp",EDGE,"E48.45");var subQ1=sQuery(id+"F2.wireOp",EDGE,"E48.31");var subQ2=makeQuery(id+"F2.imprint","INTERSECT",VERTEX,{"derivedFrom":[sQuery(id+"F2.wireOp",EDGE,"E48.0"),subQ1,subQ0]});Q7=makeQuery(id+"F2.imprint","IMPRINT",FACE,{"disambiguationData":[TD([[makeQuery(id+"F2.imprint","IMPRINT",EDGE,{"disambiguationData":[TD([[subQ2,-1.0]])],"derivedFrom":subQ1}),1.0]])]});}
            var Q8;
            {var subQ0=sQuery(id+"F2.wireOp",EDGE,"E48.32");var subQ1=sQuery(id+"F2.wireOp",EDGE,"E48.10");var subQ2=makeQuery(id+"F2.imprint","INTERSECT",VERTEX,{"derivedFrom":[sQuery(id+"F2.wireOp",EDGE,"E48.0"),subQ1,subQ0]});Q8=makeQuery(id+"F2.imprint","IMPRINT",FACE,{"disambiguationData":[TD([[makeQuery(id+"F2.imprint","IMPRINT",EDGE,{"disambiguationData":[TD([[subQ2,1.0]])],"derivedFrom":subQ1}),1.0]])]});}
            var Q9;
            {var subQ0=sQuery(id+"F2.wireOp",EDGE,"E48.38");var subQ1=sQuery(id+"F2.wireOp",EDGE,"E48.14");var subQ2=makeQuery(id+"F2.imprint","INTERSECT",VERTEX,{"derivedFrom":[sQuery(id+"F2.wireOp",EDGE,"E48.0"),subQ1,subQ0]});Q9=makeQuery(id+"F2.imprint","IMPRINT",FACE,{"disambiguationData":[TD([[makeQuery(id+"F2.imprint","IMPRINT",EDGE,{"disambiguationData":[TD([[subQ2,-1.0]])],"derivedFrom":subQ1}),1.0]])]});}
            var Q10;
            {var subQ0=sQuery(id+"F0.wireOp",EDGE,"E26");var subQ1=sQuery(id+"F0.wireOp",EDGE,"E0");var subQ2=makeQuery(id+"F0.imprint","INTERSECT",VERTEX,{"derivedFrom":[subQ1,subQ0,sQuery(id+"F0.wireOp",EDGE,"E28")]});Q10=makeQuery(id+"F0.imprint","IMPRINT",FACE,{"disambiguationData":[TD([[makeQuery(id+"F0.imprint","IMPRINT",EDGE,{"disambiguationData":[TD([[subQ2,-1.0]])],"derivedFrom":subQ1}),-1.0]])]});}
            var Q11;
            {var subQ0=sQuery(id+"F2.wireOp",EDGE,"E48.47");var subQ1=sQuery(id+"F2.wireOp",EDGE,"E48.3");var subQ2=makeQuery(id+"F2.imprint","INTERSECT",VERTEX,{"derivedFrom":[sQuery(id+"F2.wireOp",EDGE,"E48.0"),subQ1,subQ0]});Q11=makeQuery(id+"F2.imprint","IMPRINT",FACE,{"disambiguationData":[TD([[makeQuery(id+"F2.imprint","IMPRINT",EDGE,{"disambiguationData":[TD([[subQ2,-1.0]])],"derivedFrom":subQ1}),1.0]])]});}
            var Q12;
            {var subQ0=sQuery(id+"F2.wireOp",EDGE,"E48.33");var subQ1=sQuery(id+"F2.wireOp",EDGE,"E48.12");var subQ2=makeQuery(id+"F2.imprint","INTERSECT",VERTEX,{"derivedFrom":[sQuery(id+"F2.wireOp",EDGE,"E48.0"),subQ1,subQ0]});Q12=makeQuery(id+"F2.imprint","IMPRINT",FACE,{"disambiguationData":[TD([[makeQuery(id+"F2.imprint","IMPRINT",EDGE,{"disambiguationData":[TD([[subQ2,1.0]])],"derivedFrom":subQ1}),1.0]])]});}
            var Q13;
            {var subQ0=sQuery(id+"F2.wireOp",EDGE,"E48.40");var subQ1=sQuery(id+"F2.wireOp",EDGE,"E48.16");var subQ2=makeQuery(id+"F2.imprint","INTERSECT",VERTEX,{"derivedFrom":[sQuery(id+"F2.wireOp",EDGE,"E48.0"),subQ1,subQ0]});Q13=makeQuery(id+"F2.imprint","IMPRINT",FACE,{"disambiguationData":[TD([[makeQuery(id+"F2.imprint","IMPRINT",EDGE,{"disambiguationData":[TD([[subQ2,-1.0]])],"derivedFrom":subQ1}),1.0]])]});}
            var Q14;
            {var subQ0=sQuery(id+"F2.wireOp",EDGE,"E48.43");var subQ1=sQuery(id+"F2.wireOp",EDGE,"E48.31");var subQ2=makeQuery(id+"F2.imprint","INTERSECT",VERTEX,{"derivedFrom":[sQuery(id+"F2.wireOp",EDGE,"E48.0"),subQ1,subQ0]});Q14=makeQuery(id+"F2.imprint","IMPRINT",FACE,{"disambiguationData":[TD([[makeQuery(id+"F2.imprint","IMPRINT",EDGE,{"disambiguationData":[TD([[subQ2,1.0]])],"derivedFrom":subQ1}),1.0]])]});}
            var Q15;
            {var subQ0=sQuery(id+"F2.wireOp",EDGE,"E48.32");var subQ1=sQuery(id+"F2.wireOp",EDGE,"E48.2");var subQ2=makeQuery(id+"F2.imprint","INTERSECT",VERTEX,{"derivedFrom":[sQuery(id+"F2.wireOp",EDGE,"E48.0"),subQ1,subQ0]});Q15=makeQuery(id+"F2.imprint","IMPRINT",FACE,{"disambiguationData":[TD([[makeQuery(id+"F2.imprint","IMPRINT",EDGE,{"disambiguationData":[TD([[subQ2,-1.0]])],"derivedFrom":subQ1}),1.0]])]});}
            var Q16;
            {var subQ0=sQuery(id+"F2.wireOp",EDGE,"E48.34");var subQ1=sQuery(id+"F2.wireOp",EDGE,"E48.14");var subQ2=makeQuery(id+"F2.imprint","INTERSECT",VERTEX,{"derivedFrom":[sQuery(id+"F2.wireOp",EDGE,"E48.0"),subQ1,subQ0]});Q16=makeQuery(id+"F2.imprint","IMPRINT",FACE,{"disambiguationData":[TD([[makeQuery(id+"F2.imprint","IMPRINT",EDGE,{"disambiguationData":[TD([[subQ2,1.0]])],"derivedFrom":subQ1}),1.0]])]});}
            var Q17;
            {var subQ0=sQuery(id+"F2.wireOp",EDGE,"E48.42");var subQ1=sQuery(id+"F2.wireOp",EDGE,"E48.18");var subQ2=makeQuery(id+"F2.imprint","INTERSECT",VERTEX,{"derivedFrom":[sQuery(id+"F2.wireOp",EDGE,"E48.0"),subQ1,subQ0]});Q17=makeQuery(id+"F2.imprint","IMPRINT",FACE,{"disambiguationData":[TD([[makeQuery(id+"F2.imprint","IMPRINT",EDGE,{"disambiguationData":[TD([[subQ2,-1.0]])],"derivedFrom":subQ1}),1.0]])]});}
            var Q18;
            {var subQ0=sQuery(id+"F2.wireOp",EDGE,"E48.41");var subQ1=sQuery(id+"F2.wireOp",EDGE,"E48.3");var subQ2=makeQuery(id+"F2.imprint","INTERSECT",VERTEX,{"derivedFrom":[sQuery(id+"F2.wireOp",EDGE,"E48.0"),subQ1,subQ0]});Q18=makeQuery(id+"F2.imprint","IMPRINT",FACE,{"disambiguationData":[TD([[makeQuery(id+"F2.imprint","IMPRINT",EDGE,{"disambiguationData":[TD([[subQ2,1.0]])],"derivedFrom":subQ1}),1.0]])]});}
            var Q19;
            {var subQ0=sQuery(id+"F2.wireOp",EDGE,"E48.33");var subQ1=sQuery(id+"F2.wireOp",EDGE,"E48.25");var subQ2=makeQuery(id+"F2.imprint","INTERSECT",VERTEX,{"derivedFrom":[sQuery(id+"F2.wireOp",EDGE,"E48.0"),subQ1,subQ0]});Q19=makeQuery(id+"F2.imprint","IMPRINT",FACE,{"disambiguationData":[TD([[makeQuery(id+"F2.imprint","IMPRINT",EDGE,{"disambiguationData":[TD([[subQ2,-1.0]])],"derivedFrom":subQ1}),1.0]])]});}
            var Q20;
            {var subQ0=sQuery(id+"F2.wireOp",EDGE,"E48.16");var subQ1=sQuery(id+"F2.wireOp",EDGE,"E48.5");var subQ2=makeQuery(id+"F2.imprint","INTERSECT",VERTEX,{"derivedFrom":[sQuery(id+"F2.wireOp",EDGE,"E48.0"),subQ1,subQ0]});Q20=makeQuery(id+"F2.imprint","IMPRINT",FACE,{"disambiguationData":[TD([[makeQuery(id+"F2.imprint","IMPRINT",EDGE,{"disambiguationData":[TD([[subQ2,-1.0]])],"derivedFrom":subQ1}),1.0]])]});}
            var Q21;
            {var subQ0=sQuery(id+"F2.wireOp",EDGE,"E48.43");var subQ1=sQuery(id+"F2.wireOp",EDGE,"E48.21");var subQ2=makeQuery(id+"F2.imprint","INTERSECT",VERTEX,{"derivedFrom":[sQuery(id+"F2.wireOp",EDGE,"E48.0"),subQ1,subQ0]});Q21=makeQuery(id+"F2.imprint","IMPRINT",FACE,{"disambiguationData":[TD([[makeQuery(id+"F2.imprint","IMPRINT",EDGE,{"disambiguationData":[TD([[subQ2,-1.0]])],"derivedFrom":subQ1}),1.0]])]});}
            var Q22;
            {var subQ1=sQuery(id+"F2.wireOp",EDGE,"E48.2");var subQ3=sQuery(id+"F2.wireOp",EDGE,"E48.35");var subQ4=makeQuery(id+"F2.imprint","INTERSECT",VERTEX,{"derivedFrom":[subQ1,sQuery(id+"F2.wireOp",EDGE,"E48.27"),subQ3]});Q22=makeQuery(id+"F2.imprint","IMPRINT",FACE,{"disambiguationData":[TD([[makeQuery(id+"F2.imprint","IMPRINT",EDGE,{"disambiguationData":[TD([[subQ4,-1.0]])],"derivedFrom":subQ3}),-1.0]])]});}
            var Q23;
            {var subQ0=sQuery(id+"F0.wireOp",EDGE,"E14");var subQ1=sQuery(id+"F0.wireOp",EDGE,"E0");var subQ2=makeQuery(id+"F0.imprint","INTERSECT",VERTEX,{"derivedFrom":[subQ1,sQuery(id+"F0.wireOp",EDGE,"E10"),subQ0]});Q23=makeQuery(id+"F0.imprint","IMPRINT",FACE,{"disambiguationData":[TD([[makeQuery(id+"F0.imprint","IMPRINT",EDGE,{"disambiguationData":[TD([[subQ2,-1.0]])],"derivedFrom":subQ1}),-1.0]])]});}
            var Q24;
            {var subQ0=sQuery(id+"F2.wireOp",EDGE,"E48.39");var subQ4=sQuery(id+"F2.wireOp",EDGE,"E48.34");var subQ6=makeQuery(id+"F2.imprint","INTERSECT",VERTEX,{"derivedFrom":[sQuery(id+"F2.wireOp",EDGE,"E48.9"),subQ4,subQ0]});Q24=makeQuery(id+"F2.imprint","IMPRINT",FACE,{"disambiguationData":[TD([[makeQuery(id+"F2.imprint","IMPRINT",EDGE,{"disambiguationData":[TD([[subQ6,-1.0]])],"derivedFrom":subQ0}),1.0]])]});}
            var Q25;
            {var subQ0=sQuery(id+"F2.wireOp",EDGE,"E48.27");var subQ3=sQuery(id+"F2.wireOp",EDGE,"E48.18");var subQ5=makeQuery(id+"F2.imprint","INTERSECT",VERTEX,{"derivedFrom":[sQuery(id+"F2.wireOp",EDGE,"E48.9"),subQ3,subQ0]});Q25=makeQuery(id+"F2.imprint","IMPRINT",FACE,{"disambiguationData":[TD([[makeQuery(id+"F2.imprint","IMPRINT",EDGE,{"disambiguationData":[TD([[subQ5,1.0]])],"derivedFrom":subQ3}),1.0]])]});}
            var Q26;
            {var subQ0=sQuery(id+"F2.wireOp",EDGE,"E48.41");var subQ1=sQuery(id+"F2.wireOp",EDGE,"E48.0");var subQ2=makeQuery(id+"F2.imprint","INTERSECT",VERTEX,{"derivedFrom":[subQ1,sQuery(id+"F2.wireOp",EDGE,"E48.10"),subQ0]});Q26=makeQuery(id+"F2.imprint","IMPRINT",FACE,{"disambiguationData":[TD([[makeQuery(id+"F2.imprint","IMPRINT",EDGE,{"disambiguationData":[TD([[subQ2,-1.0]])],"derivedFrom":subQ0}),1.0]])]});}
            var Q27;
            {var subQ0=sQuery(id+"F2.wireOp",EDGE,"E48.25");var subQ1=sQuery(id+"F2.wireOp",EDGE,"E48.0");var subQ2=makeQuery(id+"F2.imprint","INTERSECT",VERTEX,{"derivedFrom":[subQ1,subQ0,sQuery(id+"F2.wireOp",EDGE,"E48.38")]});Q27=makeQuery(id+"F2.imprint","IMPRINT",FACE,{"disambiguationData":[TD([[makeQuery(id+"F2.imprint","IMPRINT",EDGE,{"disambiguationData":[TD([[subQ2,-1.0]])],"derivedFrom":subQ1}),-1.0]])]});}
            var Q28;
            {var subQ0=sQuery(id+"F2.wireOp",EDGE,"E48.5");var subQ1=sQuery(id+"F2.wireOp",EDGE,"E48.0");var subQ2=makeQuery(id+"F2.imprint","INTERSECT",VERTEX,{"derivedFrom":[subQ1,subQ0,sQuery(id+"F2.wireOp",EDGE,"E48.29")]});Q28=makeQuery(id+"F2.imprint","IMPRINT",FACE,{"disambiguationData":[TD([[makeQuery(id+"F2.imprint","IMPRINT",EDGE,{"disambiguationData":[TD([[subQ2,-1.0]])],"derivedFrom":subQ1}),-1.0]])]});}
            var Q29;
            {var subQ0=sQuery(id+"F0.wireOp",EDGE,"E30");var subQ1=sQuery(id+"F0.wireOp",EDGE,"E22");var subQ2=makeQuery(id+"F0.imprint","INTERSECT",VERTEX,{"derivedFrom":[sQuery(id+"F0.wireOp",EDGE,"E11"),subQ1,subQ0]});Q29=makeQuery(id+"F0.imprint","IMPRINT",FACE,{"disambiguationData":[TD([[makeQuery(id+"F0.imprint","IMPRINT",EDGE,{"disambiguationData":[TD([[subQ2,-1.0]])],"derivedFrom":subQ1}),1.0]])]});}
            var Q30;
            {var subQ0=sQuery(id+"F2.wireOp",EDGE,"E48.47");var subQ1=sQuery(id+"F2.wireOp",EDGE,"E48.0");var subQ2=makeQuery(id+"F2.imprint","INTERSECT",VERTEX,{"derivedFrom":[subQ1,sQuery(id+"F2.wireOp",EDGE,"E48.21"),subQ0]});Q30=makeQuery(id+"F2.imprint","IMPRINT",FACE,{"disambiguationData":[TD([[makeQuery(id+"F2.imprint","IMPRINT",EDGE,{"disambiguationData":[TD([[subQ2,1.0]])],"derivedFrom":subQ1}),-1.0]])]});}
            var Q31;
            {var subQ0=sQuery(id+"F2.wireOp",EDGE,"E48.12");var subQ1=sQuery(id+"F2.wireOp",EDGE,"E48.0");var subQ2=makeQuery(id+"F2.imprint","INTERSECT",VERTEX,{"derivedFrom":[subQ1,subQ0,sQuery(id+"F2.wireOp",EDGE,"E48.39")]});Q31=makeQuery(id+"F2.imprint","IMPRINT",FACE,{"disambiguationData":[TD([[makeQuery(id+"F2.imprint","IMPRINT",EDGE,{"disambiguationData":[TD([[subQ2,1.0]])],"derivedFrom":subQ1}),-1.0]])]});}
            var Q32;
            {var subQ0=sQuery(id+"F2.wireOp",EDGE,"E48.45");var subQ1=sQuery(id+"F2.wireOp",EDGE,"E48.0");var subQ2=makeQuery(id+"F2.imprint","INTERSECT",VERTEX,{"derivedFrom":[subQ1,sQuery(id+"F2.wireOp",EDGE,"E48.31"),subQ0]});Q32=makeQuery(id+"F2.imprint","IMPRINT",FACE,{"disambiguationData":[TD([[makeQuery(id+"F2.imprint","IMPRINT",EDGE,{"disambiguationData":[TD([[subQ2,-1.0]])],"derivedFrom":subQ1}),-1.0]])]});}
            var Q33;
            {var subQ0=sQuery(id+"F2.wireOp",EDGE,"E48.10");var subQ1=sQuery(id+"F2.wireOp",EDGE,"E48.0");var subQ2=makeQuery(id+"F2.imprint","INTERSECT",VERTEX,{"derivedFrom":[subQ1,subQ0,sQuery(id+"F2.wireOp",EDGE,"E48.32")]});Q33=makeQuery(id+"F2.imprint","IMPRINT",FACE,{"disambiguationData":[TD([[makeQuery(id+"F2.imprint","IMPRINT",EDGE,{"disambiguationData":[TD([[subQ2,-1.0]])],"derivedFrom":subQ1}),-1.0]])]});}
            var Q34;
            {var subQ0=sQuery(id+"F2.wireOp",EDGE,"E48.38");var subQ1=sQuery(id+"F2.wireOp",EDGE,"E48.0");var subQ2=makeQuery(id+"F2.imprint","INTERSECT",VERTEX,{"derivedFrom":[subQ1,sQuery(id+"F2.wireOp",EDGE,"E48.14"),subQ0]});Q34=makeQuery(id+"F2.imprint","IMPRINT",FACE,{"disambiguationData":[TD([[makeQuery(id+"F2.imprint","IMPRINT",EDGE,{"disambiguationData":[TD([[subQ2,-1.0]])],"derivedFrom":subQ1}),-1.0]])]});}
            var Q35;
            {var subQ0=sQuery(id+"F0.wireOp",EDGE,"E30");var subQ1=sQuery(id+"F0.wireOp",EDGE,"E19");var subQ2=makeQuery(id+"F0.imprint","INTERSECT",VERTEX,{"derivedFrom":[sQuery(id+"F0.wireOp",EDGE,"E3"),subQ1,subQ0]});Q35=makeQuery(id+"F0.imprint","IMPRINT",FACE,{"disambiguationData":[TD([[makeQuery(id+"F0.imprint","IMPRINT",EDGE,{"disambiguationData":[TD([[subQ2,1.0]])],"derivedFrom":subQ1}),1.0]])]});}
            var Q36;
            {var subQ0=sQuery(id+"F0.wireOp",EDGE,"E11");var subQ1=sQuery(id+"F0.wireOp",EDGE,"E7");var subQ2=makeQuery(id+"F0.imprint","INTERSECT",VERTEX,{"derivedFrom":[subQ1,subQ0,sQuery(id+"F0.wireOp",EDGE,"E32")]});Q36=makeQuery(id+"F0.imprint","IMPRINT",FACE,{"disambiguationData":[TD([[makeQuery(id+"F0.imprint","IMPRINT",EDGE,{"disambiguationData":[TD([[subQ2,-1.0]])],"derivedFrom":subQ1}),1.0]])]});}
            var Q37;
            {var subQ0=sQuery(id+"F2.wireOp",EDGE,"E48.12");var subQ1=sQuery(id+"F2.wireOp",EDGE,"E48.0");var subQ2=makeQuery(id+"F2.imprint","INTERSECT",VERTEX,{"derivedFrom":[subQ1,subQ0,sQuery(id+"F2.wireOp",EDGE,"E48.33")]});Q37=makeQuery(id+"F2.imprint","IMPRINT",FACE,{"disambiguationData":[TD([[makeQuery(id+"F2.imprint","IMPRINT",EDGE,{"disambiguationData":[TD([[subQ2,-1.0]])],"derivedFrom":subQ1}),-1.0]])]});}
            var Q38;
            {var subQ0=sQuery(id+"F2.wireOp",EDGE,"E48.40");var subQ1=sQuery(id+"F2.wireOp",EDGE,"E48.0");var subQ2=makeQuery(id+"F2.imprint","INTERSECT",VERTEX,{"derivedFrom":[subQ1,sQuery(id+"F2.wireOp",EDGE,"E48.16"),subQ0]});Q38=makeQuery(id+"F2.imprint","IMPRINT",FACE,{"disambiguationData":[TD([[makeQuery(id+"F2.imprint","IMPRINT",EDGE,{"disambiguationData":[TD([[subQ2,-1.0]])],"derivedFrom":subQ1}),-1.0]])]});}
            var Q39;
            {var subQ0=sQuery(id+"F2.wireOp",EDGE,"E48.31");var subQ1=sQuery(id+"F2.wireOp",EDGE,"E48.0");var subQ2=makeQuery(id+"F2.imprint","INTERSECT",VERTEX,{"derivedFrom":[subQ1,subQ0,sQuery(id+"F2.wireOp",EDGE,"E48.43")]});Q39=makeQuery(id+"F2.imprint","IMPRINT",FACE,{"disambiguationData":[TD([[makeQuery(id+"F2.imprint","IMPRINT",EDGE,{"disambiguationData":[TD([[subQ2,-1.0]])],"derivedFrom":subQ1}),-1.0]])]});}
            var Q40;
            {var subQ0=sQuery(id+"F2.wireOp",EDGE,"E48.32");var subQ1=sQuery(id+"F2.wireOp",EDGE,"E48.0");var subQ2=makeQuery(id+"F2.imprint","INTERSECT",VERTEX,{"derivedFrom":[subQ1,sQuery(id+"F2.wireOp",EDGE,"E48.2"),subQ0]});Q40=makeQuery(id+"F2.imprint","IMPRINT",FACE,{"disambiguationData":[TD([[makeQuery(id+"F2.imprint","IMPRINT",EDGE,{"disambiguationData":[TD([[subQ2,-1.0]])],"derivedFrom":subQ1}),-1.0]])]});}
            var Q41;
            {var subQ0=sQuery(id+"F2.wireOp",EDGE,"E48.14");var subQ1=sQuery(id+"F2.wireOp",EDGE,"E48.0");var subQ2=makeQuery(id+"F2.imprint","INTERSECT",VERTEX,{"derivedFrom":[subQ1,subQ0,sQuery(id+"F2.wireOp",EDGE,"E48.34")]});Q41=makeQuery(id+"F2.imprint","IMPRINT",FACE,{"disambiguationData":[TD([[makeQuery(id+"F2.imprint","IMPRINT",EDGE,{"disambiguationData":[TD([[subQ2,-1.0]])],"derivedFrom":subQ1}),-1.0]])]});}
            var Q42;
            {var subQ0=sQuery(id+"F2.wireOp",EDGE,"E48.42");var subQ1=sQuery(id+"F2.wireOp",EDGE,"E48.0");var subQ2=makeQuery(id+"F2.imprint","INTERSECT",VERTEX,{"derivedFrom":[subQ1,sQuery(id+"F2.wireOp",EDGE,"E48.18"),subQ0]});Q42=makeQuery(id+"F2.imprint","IMPRINT",FACE,{"disambiguationData":[TD([[makeQuery(id+"F2.imprint","IMPRINT",EDGE,{"disambiguationData":[TD([[subQ2,-1.0]])],"derivedFrom":subQ1}),-1.0]])]});}
            var Q43;
            {var subQ0=sQuery(id+"F0.wireOp",EDGE,"E30");var subQ1=sQuery(id+"F0.wireOp",EDGE,"E21");var subQ2=makeQuery(id+"F0.imprint","INTERSECT",VERTEX,{"derivedFrom":[sQuery(id+"F0.wireOp",EDGE,"E7"),subQ1,subQ0]});Q43=makeQuery(id+"F0.imprint","IMPRINT",FACE,{"disambiguationData":[TD([[makeQuery(id+"F0.imprint","IMPRINT",EDGE,{"disambiguationData":[TD([[subQ2,1.0]])],"derivedFrom":subQ1}),1.0]])]});}
            var Q44;
            {var subQ0=sQuery(id+"F2.wireOp",EDGE,"E48.33");var subQ1=sQuery(id+"F2.wireOp",EDGE,"E48.0");var subQ2=makeQuery(id+"F2.imprint","INTERSECT",VERTEX,{"derivedFrom":[subQ1,sQuery(id+"F2.wireOp",EDGE,"E48.25"),subQ0]});Q44=makeQuery(id+"F2.imprint","IMPRINT",FACE,{"disambiguationData":[TD([[makeQuery(id+"F2.imprint","IMPRINT",EDGE,{"disambiguationData":[TD([[subQ2,-1.0]])],"derivedFrom":subQ1}),-1.0]])]});}
            var Q45;
            {var subQ0=sQuery(id+"F0.wireOp",EDGE,"E30");var subQ1=sQuery(id+"F0.wireOp",EDGE,"E20");var subQ2=makeQuery(id+"F0.imprint","INTERSECT",VERTEX,{"derivedFrom":[sQuery(id+"F0.wireOp",EDGE,"E15"),subQ1,subQ0]});Q45=makeQuery(id+"F0.imprint","IMPRINT",FACE,{"disambiguationData":[TD([[makeQuery(id+"F0.imprint","IMPRINT",EDGE,{"disambiguationData":[TD([[subQ2,-1.0]])],"derivedFrom":subQ1}),1.0]])]});}
            var Q46;
            {var subQ0=sQuery(id+"F2.wireOp",EDGE,"E48.43");var subQ1=sQuery(id+"F2.wireOp",EDGE,"E48.0");var subQ2=makeQuery(id+"F2.imprint","INTERSECT",VERTEX,{"derivedFrom":[subQ1,sQuery(id+"F2.wireOp",EDGE,"E48.21"),subQ0]});Q46=makeQuery(id+"F2.imprint","IMPRINT",FACE,{"disambiguationData":[TD([[makeQuery(id+"F2.imprint","IMPRINT",EDGE,{"disambiguationData":[TD([[subQ2,-1.0]])],"derivedFrom":subQ1}),-1.0]])]});}
            var Q47;
            {var subQ1=sQuery(id+"F2.wireOp",EDGE,"E48.0");var subQ3=sQuery(id+"F2.wireOp",EDGE,"E48.21");var subQ4=makeQuery(id+"F2.imprint","INTERSECT",VERTEX,{"derivedFrom":[subQ1,subQ3,sQuery(id+"F2.wireOp",EDGE,"E48.43")]});Q47=makeQuery(id+"F2.imprint","IMPRINT",FACE,{"disambiguationData":[TD([[makeQuery(id+"F2.imprint","IMPRINT",EDGE,{"disambiguationData":[TD([[subQ4,1.0]])],"derivedFrom":subQ3}),1.0]])]});}
            var Q48;
            {var subQ0=sQuery(id+"F0.wireOp",EDGE,"E21");var subQ1=sQuery(id+"F0.wireOp",EDGE,"E4");var subQ2=makeQuery(id+"F0.imprint","INTERSECT",VERTEX,{"derivedFrom":[subQ1,subQ0,sQuery(id+"F0.wireOp",EDGE,"E36")]});Q48=makeQuery(id+"F0.imprint","IMPRINT",FACE,{"disambiguationData":[TD([[makeQuery(id+"F0.imprint","IMPRINT",EDGE,{"disambiguationData":[TD([[subQ2,-1.0]])],"derivedFrom":subQ1}),1.0]])]});}
            var Q49;
            {var subQ0=sQuery(id+"F2.wireOp",EDGE,"E48.25");var subQ1=sQuery(id+"F2.wireOp",EDGE,"E48.9");var subQ2=makeQuery(id+"F2.imprint","INTERSECT",VERTEX,{"derivedFrom":[subQ1,sQuery(id+"F2.wireOp",EDGE,"E48.10"),subQ0]});Q49=makeQuery(id+"F2.imprint","IMPRINT",FACE,{"disambiguationData":[TD([[makeQuery(id+"F2.imprint","IMPRINT",EDGE,{"disambiguationData":[TD([[subQ2,-1.0]])],"derivedFrom":subQ1}),-1.0]])]});}
            var Q50;
            {var subQ0=sQuery(id+"F2.wireOp",EDGE,"E48.10");var subQ1=sQuery(id+"F2.wireOp",EDGE,"E48.5");var subQ2=makeQuery(id+"F2.imprint","INTERSECT",VERTEX,{"derivedFrom":[subQ1,subQ0,sQuery(id+"F2.wireOp",EDGE,"E48.17")]});Q50=makeQuery(id+"F2.imprint","IMPRINT",FACE,{"disambiguationData":[TD([[makeQuery(id+"F2.imprint","IMPRINT",EDGE,{"disambiguationData":[TD([[subQ2,1.0]])],"derivedFrom":subQ1}),1.0]])]});}
            var Q51;
            {var subQ0=sQuery(id+"F2.wireOp",EDGE,"E48.38");var subQ1=sQuery(id+"F2.wireOp",EDGE,"E48.9");var subQ2=makeQuery(id+"F2.imprint","INTERSECT",VERTEX,{"derivedFrom":[sQuery(id+"F2.wireOp",EDGE,"E48.5"),subQ1,subQ0]});Q51=makeQuery(id+"F2.imprint","IMPRINT",FACE,{"disambiguationData":[TD([[makeQuery(id+"F2.imprint","IMPRINT",EDGE,{"disambiguationData":[TD([[subQ2,1.0]])],"derivedFrom":subQ1}),-1.0]])]});}
            var Q52;
            {var subQ0=sQuery(id+"F2.wireOp",EDGE,"E48.39");var subQ1=sQuery(id+"F2.wireOp",EDGE,"E48.9");var subQ2=makeQuery(id+"F2.imprint","INTERSECT",VERTEX,{"derivedFrom":[subQ1,subQ0,sQuery(id+"F2.wireOp",EDGE,"E48.47")]});Q52=makeQuery(id+"F2.imprint","IMPRINT",FACE,{"disambiguationData":[TD([[makeQuery(id+"F2.imprint","IMPRINT",EDGE,{"disambiguationData":[TD([[subQ2,-1.0]])],"derivedFrom":subQ1}),-1.0]])]});}
            var Q53;
            {var subQ0=sQuery(id+"F0.wireOp",EDGE,"E32");var subQ1=sQuery(id+"F0.wireOp",EDGE,"E11");var subQ2=makeQuery(id+"F0.imprint","INTERSECT",VERTEX,{"derivedFrom":[sQuery(id+"F0.wireOp",EDGE,"E4"),subQ1,subQ0]});Q53=makeQuery(id+"F0.imprint","IMPRINT",FACE,{"disambiguationData":[TD([[makeQuery(id+"F0.imprint","IMPRINT",EDGE,{"disambiguationData":[TD([[subQ2,1.0]])],"derivedFrom":subQ1}),1.0]])]});}
            var Q54;
            {var subQ0=sQuery(id+"F2.wireOp",EDGE,"E48.12");var subQ1=sQuery(id+"F2.wireOp",EDGE,"E48.9");var subQ2=makeQuery(id+"F2.imprint","INTERSECT",VERTEX,{"derivedFrom":[subQ1,subQ0,sQuery(id+"F2.wireOp",EDGE,"E48.27")]});Q54=makeQuery(id+"F2.imprint","IMPRINT",FACE,{"disambiguationData":[TD([[makeQuery(id+"F2.imprint","IMPRINT",EDGE,{"disambiguationData":[TD([[subQ2,1.0]])],"derivedFrom":subQ1}),-1.0]])]});}
            var Q55;
            {var subQ0=sQuery(id+"F2.wireOp",EDGE,"E48.10");var subQ1=sQuery(id+"F2.wireOp",EDGE,"E48.9");var subQ2=makeQuery(id+"F2.imprint","INTERSECT",VERTEX,{"derivedFrom":[subQ1,subQ0,sQuery(id+"F2.wireOp",EDGE,"E48.31")]});Q55=makeQuery(id+"F2.imprint","IMPRINT",FACE,{"disambiguationData":[TD([[makeQuery(id+"F2.imprint","IMPRINT",EDGE,{"disambiguationData":[TD([[subQ2,-1.0]])],"derivedFrom":subQ1}),-1.0]])]});}
            var Q56;
            {var subQ0=sQuery(id+"F2.wireOp",EDGE,"E48.38");var subQ1=sQuery(id+"F2.wireOp",EDGE,"E48.9");var subQ2=makeQuery(id+"F2.imprint","INTERSECT",VERTEX,{"derivedFrom":[subQ1,sQuery(id+"F2.wireOp",EDGE,"E48.32"),subQ0]});Q56=makeQuery(id+"F2.imprint","IMPRINT",FACE,{"disambiguationData":[TD([[makeQuery(id+"F2.imprint","IMPRINT",EDGE,{"disambiguationData":[TD([[subQ2,-1.0]])],"derivedFrom":subQ1}),-1.0]])]});}
            var Q57;
            {var subQ0=sQuery(id+"F2.wireOp",EDGE,"E48.29");var subQ1=sQuery(id+"F2.wireOp",EDGE,"E48.9");var subQ2=makeQuery(id+"F2.imprint","INTERSECT",VERTEX,{"derivedFrom":[subQ1,sQuery(id+"F2.wireOp",EDGE,"E48.14"),subQ0]});Q57=makeQuery(id+"F2.imprint","IMPRINT",FACE,{"disambiguationData":[TD([[makeQuery(id+"F2.imprint","IMPRINT",EDGE,{"disambiguationData":[TD([[subQ2,-1.0]])],"derivedFrom":subQ1}),-1.0]])]});}
            var Q58;
            {var subQ0=sQuery(id+"F0.wireOp",EDGE,"E32");var subQ1=sQuery(id+"F0.wireOp",EDGE,"E11");var subQ2=makeQuery(id+"F0.imprint","INTERSECT",VERTEX,{"derivedFrom":[sQuery(id+"F0.wireOp",EDGE,"E7"),subQ1,subQ0]});Q58=makeQuery(id+"F0.imprint","IMPRINT",FACE,{"disambiguationData":[TD([[makeQuery(id+"F0.imprint","IMPRINT",EDGE,{"disambiguationData":[TD([[subQ2,-1.0]])],"derivedFrom":subQ1}),1.0]])]});}
            var Q59;
            {var subQ0=sQuery(id+"F0.wireOp",EDGE,"E18");var subQ1=sQuery(id+"F0.wireOp",EDGE,"E7");var subQ2=makeQuery(id+"F0.imprint","INTERSECT",VERTEX,{"derivedFrom":[subQ1,subQ0,sQuery(id+"F0.wireOp",EDGE,"E36")]});Q59=makeQuery(id+"F0.imprint","IMPRINT",FACE,{"disambiguationData":[TD([[makeQuery(id+"F0.imprint","IMPRINT",EDGE,{"disambiguationData":[TD([[subQ2,-1.0]])],"derivedFrom":subQ1}),1.0]])]});}
            var Q60;
            {var subQ0=sQuery(id+"F2.wireOp",EDGE,"E48.40");var subQ1=sQuery(id+"F2.wireOp",EDGE,"E48.3");var subQ2=makeQuery(id+"F2.imprint","INTERSECT",VERTEX,{"derivedFrom":[subQ1,sQuery(id+"F2.wireOp",EDGE,"E48.17"),subQ0]});Q60=makeQuery(id+"F2.imprint","IMPRINT",FACE,{"disambiguationData":[TD([[makeQuery(id+"F2.imprint","IMPRINT",EDGE,{"disambiguationData":[TD([[subQ2,-1.0]])],"derivedFrom":subQ1}),1.0]])]});}
            var Q61;
            {var subQ0=sQuery(id+"F0.wireOp",EDGE,"E32");var subQ1=sQuery(id+"F0.wireOp",EDGE,"E13");var subQ2=makeQuery(id+"F0.imprint","INTERSECT",VERTEX,{"derivedFrom":[sQuery(id+"F0.wireOp",EDGE,"E5"),subQ1,subQ0]});Q61=makeQuery(id+"F0.imprint","IMPRINT",FACE,{"disambiguationData":[TD([[makeQuery(id+"F0.imprint","IMPRINT",EDGE,{"disambiguationData":[TD([[subQ2,1.0]])],"derivedFrom":subQ1}),1.0]])]});}
            var Q62;
            {var subQ0=sQuery(id+"F2.wireOp",EDGE,"E48.32");var subQ1=sQuery(id+"F2.wireOp",EDGE,"E48.9");var subQ2=makeQuery(id+"F2.imprint","INTERSECT",VERTEX,{"derivedFrom":[subQ1,subQ0,sQuery(id+"F2.wireOp",EDGE,"E48.43")]});Q62=makeQuery(id+"F2.imprint","IMPRINT",FACE,{"disambiguationData":[TD([[makeQuery(id+"F2.imprint","IMPRINT",EDGE,{"disambiguationData":[TD([[subQ2,-1.0]])],"derivedFrom":subQ1}),-1.0]])]});}
            var Q63;
            {var subQ0=sQuery(id+"F2.wireOp",EDGE,"E48.14");var subQ1=sQuery(id+"F2.wireOp",EDGE,"E48.9");var subQ2=makeQuery(id+"F2.imprint","INTERSECT",VERTEX,{"derivedFrom":[sQuery(id+"F2.wireOp",EDGE,"E48.2"),subQ1,subQ0]});Q63=makeQuery(id+"F2.imprint","IMPRINT",FACE,{"disambiguationData":[TD([[makeQuery(id+"F2.imprint","IMPRINT",EDGE,{"disambiguationData":[TD([[subQ2,-1.0]])],"derivedFrom":subQ1}),-1.0]])]});}
            var Q64;
            {var subQ0=sQuery(id+"F0.wireOp",EDGE,"E32");var subQ1=sQuery(id+"F0.wireOp",EDGE,"E7");var subQ2=makeQuery(id+"F0.imprint","INTERSECT",VERTEX,{"derivedFrom":[subQ1,sQuery(id+"F0.wireOp",EDGE,"E14"),subQ0]});Q64=makeQuery(id+"F0.imprint","IMPRINT",FACE,{"disambiguationData":[TD([[makeQuery(id+"F0.imprint","IMPRINT",EDGE,{"disambiguationData":[TD([[subQ2,-1.0]])],"derivedFrom":subQ1}),1.0]])]});}
            var Q65;
            {var subQ0=sQuery(id+"F2.wireOp",EDGE,"E48.9");var subQ1=sQuery(id+"F2.wireOp",EDGE,"E48.3");var subQ2=makeQuery(id+"F2.imprint","INTERSECT",VERTEX,{"derivedFrom":[subQ1,subQ0,sQuery(id+"F2.wireOp",EDGE,"E48.18")]});Q65=makeQuery(id+"F2.imprint","IMPRINT",FACE,{"disambiguationData":[TD([[makeQuery(id+"F2.imprint","IMPRINT",EDGE,{"disambiguationData":[TD([[subQ2,-1.0]])],"derivedFrom":subQ1}),1.0]])]});}
            var Q66;
            {var subQ0=sQuery(id+"F2.wireOp",EDGE,"E48.18");var subQ1=sQuery(id+"F2.wireOp",EDGE,"E48.9");var subQ2=makeQuery(id+"F2.imprint","INTERSECT",VERTEX,{"derivedFrom":[sQuery(id+"F2.wireOp",EDGE,"E48.3"),subQ1,subQ0]});Q66=makeQuery(id+"F2.imprint","IMPRINT",FACE,{"disambiguationData":[TD([[makeQuery(id+"F2.imprint","IMPRINT",EDGE,{"disambiguationData":[TD([[subQ2,1.0]])],"derivedFrom":subQ1}),-1.0]])]});}
            var Q67;
            {var subQ0=sQuery(id+"F2.wireOp",EDGE,"E48.43");var subQ1=sQuery(id+"F2.wireOp",EDGE,"E48.9");var subQ2=makeQuery(id+"F2.imprint","INTERSECT",VERTEX,{"derivedFrom":[sQuery(id+"F2.wireOp",EDGE,"E48.5"),subQ1,subQ0]});Q67=makeQuery(id+"F2.imprint","IMPRINT",FACE,{"disambiguationData":[TD([[makeQuery(id+"F2.imprint","IMPRINT",EDGE,{"disambiguationData":[TD([[subQ2,-1.0]])],"derivedFrom":subQ1}),-1.0]])]});}
            var Q68;
            {var subQ0=sQuery(id+"F2.wireOp",EDGE,"E48.9");var subQ1=sQuery(id+"F2.wireOp",EDGE,"E48.2");var subQ2=makeQuery(id+"F2.imprint","INTERSECT",VERTEX,{"derivedFrom":[subQ1,subQ0,sQuery(id+"F2.wireOp",EDGE,"E48.21")]});Q68=makeQuery(id+"F2.imprint","IMPRINT",FACE,{"disambiguationData":[TD([[makeQuery(id+"F2.imprint","IMPRINT",EDGE,{"disambiguationData":[TD([[subQ2,-1.0]])],"derivedFrom":subQ1}),1.0]])]});}
            var Q69;
            {var subQ0=sQuery(id+"F2.wireOp",EDGE,"E48.16");var subQ1=sQuery(id+"F2.wireOp",EDGE,"E48.9");var subQ2=makeQuery(id+"F2.imprint","INTERSECT",VERTEX,{"derivedFrom":[subQ1,subQ0,sQuery(id+"F2.wireOp",EDGE,"E48.25")]});Q69=makeQuery(id+"F2.imprint","IMPRINT",FACE,{"disambiguationData":[TD([[makeQuery(id+"F2.imprint","IMPRINT",EDGE,{"disambiguationData":[TD([[subQ2,-1.0]])],"derivedFrom":subQ1}),-1.0]])]});}
            var Q70;
            {var subQ0=sQuery(id+"F2.wireOp",EDGE,"E48.21");var subQ1=sQuery(id+"F2.wireOp",EDGE,"E48.9");var subQ2=makeQuery(id+"F2.imprint","INTERSECT",VERTEX,{"derivedFrom":[sQuery(id+"F2.wireOp",EDGE,"E48.2"),subQ1,subQ0]});Q70=makeQuery(id+"F2.imprint","IMPRINT",FACE,{"disambiguationData":[TD([[makeQuery(id+"F2.imprint","IMPRINT",EDGE,{"disambiguationData":[TD([[subQ2,1.0]])],"derivedFrom":subQ1}),-1.0]])]});}
            var Q71;
            {var subQ0=sQuery(id+"F2.wireOp",EDGE,"E48.15");var subQ1=sQuery(id+"F2.wireOp",EDGE,"E48.9");var subQ2=makeQuery(id+"F2.imprint","INTERSECT",VERTEX,{"derivedFrom":[subQ1,subQ0]});Q71=makeQuery(id+"F2.imprint","IMPRINT",FACE,{"disambiguationData":[TD([[makeQuery(id+"F2.imprint","IMPRINT",EDGE,{"disambiguationData":[TD([[subQ2,1.0]])],"derivedFrom":subQ1}),-1.0]])]});}
            var Q72;
            {var subQ0=sQuery(id+"F2.wireOp",EDGE,"E48.15");var subQ1=sQuery(id+"F2.wireOp",EDGE,"E48.9");var subQ2=makeQuery(id+"F2.imprint","INTERSECT",VERTEX,{"derivedFrom":[subQ1,subQ0]});Q72=makeQuery(id+"F2.imprint","IMPRINT",FACE,{"disambiguationData":[TD([[makeQuery(id+"F2.imprint","IMPRINT",EDGE,{"disambiguationData":[TD([[subQ2,-1.0]])],"derivedFrom":subQ1}),-1.0]])]});}
            var Q73;
            {var subQ1=sQuery(id+"F2.wireOp",EDGE,"E48.17");var subQ3=sQuery(id+"F2.wireOp",EDGE,"E48.25");var subQ4=makeQuery(id+"F2.imprint","INTERSECT",VERTEX,{"derivedFrom":[subQ1,subQ3,sQuery(id+"F2.wireOp",EDGE,"E48.45")]});Q73=makeQuery(id+"F2.imprint","IMPRINT",FACE,{"disambiguationData":[TD([[makeQuery(id+"F2.imprint","IMPRINT",EDGE,{"disambiguationData":[TD([[subQ4,-1.0]])],"derivedFrom":subQ3}),1.0]])]});}
            var Q74;
            {var subQ0=sQuery(id+"F2.wireOp",EDGE,"E48.41");var subQ3=sQuery(id+"F2.wireOp",EDGE,"E48.39");var subQ5=makeQuery(id+"F2.imprint","INTERSECT",VERTEX,{"derivedFrom":[sQuery(id+"F2.wireOp",EDGE,"E48.24"),subQ3,subQ0]});Q74=makeQuery(id+"F2.imprint","IMPRINT",FACE,{"disambiguationData":[TD([[makeQuery(id+"F2.imprint","IMPRINT",EDGE,{"disambiguationData":[TD([[subQ5,-1.0]])],"derivedFrom":subQ3}),1.0]])]});}
            var Q75;
            {var subQ0=sQuery(id+"F2.wireOp",EDGE,"E48.21");var subQ1=sQuery(id+"F2.wireOp",EDGE,"E48.17");var subQ2=makeQuery(id+"F2.imprint","INTERSECT",VERTEX,{"derivedFrom":[subQ1,subQ0,sQuery(id+"F2.wireOp",EDGE,"E48.34")]});Q75=makeQuery(id+"F2.imprint","IMPRINT",FACE,{"disambiguationData":[TD([[makeQuery(id+"F2.imprint","IMPRINT",EDGE,{"disambiguationData":[TD([[subQ2,1.0]])],"derivedFrom":subQ0}),1.0]])]});}
            var Q76;
            {var subQ0=sQuery(id+"F2.wireOp",EDGE,"E48.17");var subQ1=sQuery(id+"F2.wireOp",EDGE,"E48.5");var subQ2=makeQuery(id+"F2.imprint","INTERSECT",VERTEX,{"derivedFrom":[sQuery(id+"F2.wireOp",EDGE,"E48.2"),subQ1,subQ0]});Q76=makeQuery(id+"F2.imprint","IMPRINT",FACE,{"disambiguationData":[TD([[makeQuery(id+"F2.imprint","IMPRINT",EDGE,{"disambiguationData":[TD([[subQ2,1.0]])],"derivedFrom":subQ1}),1.0]])]});}
            var Q77;
            {var subQ0=sQuery(id+"F2.wireOp",EDGE,"E48.17");var subQ1=sQuery(id+"F2.wireOp",EDGE,"E48.2");var subQ2=makeQuery(id+"F2.imprint","INTERSECT",VERTEX,{"derivedFrom":[subQ1,sQuery(id+"F2.wireOp",EDGE,"E48.5"),subQ0]});Q77=makeQuery(id+"F2.imprint","IMPRINT",FACE,{"disambiguationData":[TD([[makeQuery(id+"F2.imprint","IMPRINT",EDGE,{"disambiguationData":[TD([[subQ2,-1.0]])],"derivedFrom":subQ1}),1.0]])]});}
            var Q78;
            {var subQ0=sQuery(id+"F2.wireOp",EDGE,"E48.41");var subQ1=sQuery(id+"F2.wireOp",EDGE,"E48.17");var subQ2=makeQuery(id+"F2.imprint","INTERSECT",VERTEX,{"derivedFrom":[sQuery(id+"F2.wireOp",EDGE,"E48.16"),subQ1,subQ0]});Q78=makeQuery(id+"F2.imprint","IMPRINT",FACE,{"disambiguationData":[TD([[makeQuery(id+"F2.imprint","IMPRINT",EDGE,{"disambiguationData":[TD([[subQ2,1.0]])],"derivedFrom":subQ1}),-1.0]])]});}
            var Q79;
            {var subQ0=sQuery(id+"F2.wireOp",EDGE,"E48.17");var subQ1=sQuery(id+"F2.wireOp",EDGE,"E48.16");var subQ2=makeQuery(id+"F2.imprint","INTERSECT",VERTEX,{"derivedFrom":[subQ1,subQ0,sQuery(id+"F2.wireOp",EDGE,"E48.41")]});Q79=makeQuery(id+"F2.imprint","IMPRINT",FACE,{"disambiguationData":[TD([[makeQuery(id+"F2.imprint","IMPRINT",EDGE,{"disambiguationData":[TD([[subQ2,-1.0]])],"derivedFrom":subQ1}),1.0]])]});}
            var Q80;
            {var subQ0=sQuery(id+"F2.wireOp",EDGE,"E48.34");var subQ1=sQuery(id+"F2.wireOp",EDGE,"E48.17");var subQ2=makeQuery(id+"F2.imprint","INTERSECT",VERTEX,{"derivedFrom":[sQuery(id+"F2.wireOp",EDGE,"E48.3"),subQ1,subQ0]});Q80=makeQuery(id+"F2.imprint","IMPRINT",FACE,{"disambiguationData":[TD([[makeQuery(id+"F2.imprint","IMPRINT",EDGE,{"disambiguationData":[TD([[subQ2,1.0]])],"derivedFrom":subQ1}),-1.0]])]});}
            var Q81;
            {var subQ0=sQuery(id+"F2.wireOp",EDGE,"E48.17");var subQ1=sQuery(id+"F2.wireOp",EDGE,"E48.5");var subQ2=makeQuery(id+"F2.imprint","INTERSECT",VERTEX,{"derivedFrom":[subQ1,sQuery(id+"F2.wireOp",EDGE,"E48.10"),subQ0]});Q81=makeQuery(id+"F2.imprint","IMPRINT",FACE,{"disambiguationData":[TD([[makeQuery(id+"F2.imprint","IMPRINT",EDGE,{"disambiguationData":[TD([[subQ2,-1.0]])],"derivedFrom":subQ1}),1.0]])]});}
            var Q82;
            {var subQ0=sQuery(id+"F2.wireOp",EDGE,"E48.17");var subQ1=sQuery(id+"F2.wireOp",EDGE,"E48.10");var subQ2=makeQuery(id+"F2.imprint","INTERSECT",VERTEX,{"derivedFrom":[sQuery(id+"F2.wireOp",EDGE,"E48.5"),subQ1,subQ0]});Q82=makeQuery(id+"F2.imprint","IMPRINT",FACE,{"disambiguationData":[TD([[makeQuery(id+"F2.imprint","IMPRINT",EDGE,{"disambiguationData":[TD([[subQ2,1.0]])],"derivedFrom":subQ1}),1.0]])]});}
            var Q83;
            {var subQ0=sQuery(id+"F0.wireOp",EDGE,"E4");var subQ1=sQuery(id+"F0.wireOp",EDGE,"E3");var subQ2=makeQuery(id+"F0.imprint","INTERSECT",VERTEX,{"derivedFrom":[subQ1,subQ0,sQuery(id+"F0.wireOp",EDGE,"E40")]});Q83=makeQuery(id+"F0.imprint","IMPRINT",FACE,{"disambiguationData":[TD([[makeQuery(id+"F0.imprint","IMPRINT",EDGE,{"disambiguationData":[TD([[subQ2,-1.0]])],"derivedFrom":subQ1}),1.0]])]});}
            var Q84;
            {var subQ0=sQuery(id+"F0.wireOp",EDGE,"E36");var subQ1=sQuery(id+"F0.wireOp",EDGE,"E25");var subQ2=makeQuery(id+"F0.imprint","INTERSECT",VERTEX,{"derivedFrom":[sQuery(id+"F0.wireOp",EDGE,"E11"),subQ1,subQ0]});Q84=makeQuery(id+"F0.imprint","IMPRINT",FACE,{"disambiguationData":[TD([[makeQuery(id+"F0.imprint","IMPRINT",EDGE,{"disambiguationData":[TD([[subQ2,-1.0]])],"derivedFrom":subQ1}),1.0]])]});}
            var Q85;
            {var subQ0=sQuery(id+"F2.wireOp",EDGE,"E48.45");var subQ1=sQuery(id+"F2.wireOp",EDGE,"E48.17");var subQ2=makeQuery(id+"F2.imprint","INTERSECT",VERTEX,{"derivedFrom":[sQuery(id+"F2.wireOp",EDGE,"E48.12"),subQ1,subQ0]});Q85=makeQuery(id+"F2.imprint","IMPRINT",FACE,{"disambiguationData":[TD([[makeQuery(id+"F2.imprint","IMPRINT",EDGE,{"disambiguationData":[TD([[subQ2,-1.0]])],"derivedFrom":subQ1}),-1.0]])]});}
            var Q86;
            {var subQ0=sQuery(id+"F2.wireOp",EDGE,"E48.17");var subQ1=sQuery(id+"F2.wireOp",EDGE,"E48.10");var subQ2=makeQuery(id+"F2.imprint","INTERSECT",VERTEX,{"derivedFrom":[subQ1,subQ0,sQuery(id+"F2.wireOp",EDGE,"E48.40")]});Q86=makeQuery(id+"F2.imprint","IMPRINT",FACE,{"disambiguationData":[TD([[makeQuery(id+"F2.imprint","IMPRINT",EDGE,{"disambiguationData":[TD([[subQ2,-1.0]])],"derivedFrom":subQ1}),1.0]])]});}
            var Q87;
            {var subQ0=sQuery(id+"F2.wireOp",EDGE,"E48.40");var subQ1=sQuery(id+"F2.wireOp",EDGE,"E48.17");var subQ2=makeQuery(id+"F2.imprint","INTERSECT",VERTEX,{"derivedFrom":[sQuery(id+"F2.wireOp",EDGE,"E48.10"),subQ1,subQ0]});Q87=makeQuery(id+"F2.imprint","IMPRINT",FACE,{"disambiguationData":[TD([[makeQuery(id+"F2.imprint","IMPRINT",EDGE,{"disambiguationData":[TD([[subQ2,1.0]])],"derivedFrom":subQ1}),-1.0]])]});}
            var Q88;
            {var subQ0=sQuery(id+"F0.wireOp",EDGE,"E36");var subQ1=sQuery(id+"F0.wireOp",EDGE,"E28");var subQ2=makeQuery(id+"F0.imprint","INTERSECT",VERTEX,{"derivedFrom":[sQuery(id+"F0.wireOp",EDGE,"E14"),subQ1,subQ0]});Q88=makeQuery(id+"F0.imprint","IMPRINT",FACE,{"disambiguationData":[TD([[makeQuery(id+"F0.imprint","IMPRINT",EDGE,{"disambiguationData":[TD([[subQ2,-1.0]])],"derivedFrom":subQ1}),1.0]])]});}
            var Q89;
            {var subQ0=sQuery(id+"F0.wireOp",EDGE,"E36");var subQ1=sQuery(id+"F0.wireOp",EDGE,"E7");var subQ2=makeQuery(id+"F0.imprint","INTERSECT",VERTEX,{"derivedFrom":[subQ1,sQuery(id+"F0.wireOp",EDGE,"E29"),subQ0]});Q89=makeQuery(id+"F0.imprint","IMPRINT",FACE,{"disambiguationData":[TD([[makeQuery(id+"F0.imprint","IMPRINT",EDGE,{"disambiguationData":[TD([[subQ2,-1.0]])],"derivedFrom":subQ1}),1.0]])]});}
            var Q90;
            {var subQ0=sQuery(id+"F2.wireOp",EDGE,"E48.17");var subQ1=sQuery(id+"F2.wireOp",EDGE,"E48.14");var subQ2=makeQuery(id+"F2.imprint","INTERSECT",VERTEX,{"derivedFrom":[subQ1,subQ0,sQuery(id+"F2.wireOp",EDGE,"E48.43")]});Q90=makeQuery(id+"F2.imprint","IMPRINT",FACE,{"disambiguationData":[TD([[makeQuery(id+"F2.imprint","IMPRINT",EDGE,{"disambiguationData":[TD([[subQ2,-1.0]])],"derivedFrom":subQ1}),1.0]])]});}
            var Q91;
            {var subQ0=sQuery(id+"F2.wireOp",EDGE,"E48.29");var subQ1=sQuery(id+"F2.wireOp",EDGE,"E48.17");var subQ2=makeQuery(id+"F2.imprint","INTERSECT",VERTEX,{"derivedFrom":[subQ1,subQ0,sQuery(id+"F2.wireOp",EDGE,"E48.32")]});Q91=makeQuery(id+"F2.imprint","IMPRINT",FACE,{"disambiguationData":[TD([[makeQuery(id+"F2.imprint","IMPRINT",EDGE,{"disambiguationData":[TD([[subQ2,-1.0]])],"derivedFrom":subQ1}),-1.0]])]});}
            var Q92;
            {var subQ0=sQuery(id+"F2.wireOp",EDGE,"E48.47");var subQ1=sQuery(id+"F2.wireOp",EDGE,"E48.17");var subQ2=makeQuery(id+"F2.imprint","INTERSECT",VERTEX,{"derivedFrom":[sQuery(id+"F2.wireOp",EDGE,"E48.14"),subQ1,subQ0]});Q92=makeQuery(id+"F2.imprint","IMPRINT",FACE,{"disambiguationData":[TD([[makeQuery(id+"F2.imprint","IMPRINT",EDGE,{"disambiguationData":[TD([[subQ2,-1.0]])],"derivedFrom":subQ1}),-1.0]])]});}
            var Q93;
            {var subQ0=sQuery(id+"F2.wireOp",EDGE,"E48.17");var subQ1=sQuery(id+"F2.wireOp",EDGE,"E48.12");var subQ2=makeQuery(id+"F2.imprint","INTERSECT",VERTEX,{"derivedFrom":[subQ1,subQ0,sQuery(id+"F2.wireOp",EDGE,"E48.42")]});Q93=makeQuery(id+"F2.imprint","IMPRINT",FACE,{"disambiguationData":[TD([[makeQuery(id+"F2.imprint","IMPRINT",EDGE,{"disambiguationData":[TD([[subQ2,-1.0]])],"derivedFrom":subQ1}),1.0]])]});}
            var Q94;
            {var subQ0=sQuery(id+"F2.wireOp",EDGE,"E48.40");var subQ1=sQuery(id+"F2.wireOp",EDGE,"E48.17");var subQ2=makeQuery(id+"F2.imprint","INTERSECT",VERTEX,{"derivedFrom":[sQuery(id+"F2.wireOp",EDGE,"E48.3"),subQ1,subQ0]});Q94=makeQuery(id+"F2.imprint","IMPRINT",FACE,{"disambiguationData":[TD([[makeQuery(id+"F2.imprint","IMPRINT",EDGE,{"disambiguationData":[TD([[subQ2,-1.0]])],"derivedFrom":subQ1}),-1.0]])]});}
            var Q95;
            {var subQ0=sQuery(id+"F2.wireOp",EDGE,"E48.31");var subQ1=sQuery(id+"F2.wireOp",EDGE,"E48.3");var subQ2=makeQuery(id+"F2.imprint","INTERSECT",VERTEX,{"derivedFrom":[subQ1,sQuery(id+"F2.wireOp",EDGE,"E48.24"),subQ0]});Q95=makeQuery(id+"F2.imprint","IMPRINT",FACE,{"disambiguationData":[TD([[makeQuery(id+"F2.imprint","IMPRINT",EDGE,{"disambiguationData":[TD([[subQ2,-1.0]])],"derivedFrom":subQ1}),1.0]])]});}
            var Q96;
            {var subQ0=sQuery(id+"F2.wireOp",EDGE,"E48.32");var subQ1=sQuery(id+"F2.wireOp",EDGE,"E48.17");var subQ2=makeQuery(id+"F2.imprint","INTERSECT",VERTEX,{"derivedFrom":[sQuery(id+"F2.wireOp",EDGE,"E48.16"),subQ1,subQ0]});Q96=makeQuery(id+"F2.imprint","IMPRINT",FACE,{"disambiguationData":[TD([[makeQuery(id+"F2.imprint","IMPRINT",EDGE,{"disambiguationData":[TD([[subQ2,-1.0]])],"derivedFrom":subQ1}),-1.0]])]});}
            var Q97;
            {var subQ0=sQuery(id+"F2.wireOp",EDGE,"E48.18");var subQ1=sQuery(id+"F2.wireOp",EDGE,"E48.5");var subQ2=makeQuery(id+"F2.imprint","INTERSECT",VERTEX,{"derivedFrom":[subQ1,subQ0,sQuery(id+"F2.wireOp",EDGE,"E48.20")]});Q97=makeQuery(id+"F2.imprint","IMPRINT",FACE,{"disambiguationData":[TD([[makeQuery(id+"F2.imprint","IMPRINT",EDGE,{"disambiguationData":[TD([[subQ2,-1.0]])],"derivedFrom":subQ1}),1.0]])]});}
            var Q98;
            {var subQ0=sQuery(id+"F2.wireOp",EDGE,"E48.25");var subQ1=sQuery(id+"F2.wireOp",EDGE,"E48.24");var subQ2=makeQuery(id+"F2.imprint","INTERSECT",VERTEX,{"derivedFrom":[sQuery(id+"F2.wireOp",EDGE,"E48.2"),subQ1,subQ0]});Q98=makeQuery(id+"F2.imprint","IMPRINT",FACE,{"disambiguationData":[TD([[makeQuery(id+"F2.imprint","IMPRINT",EDGE,{"disambiguationData":[TD([[subQ2,1.0]])],"derivedFrom":subQ1}),-1.0]])]});}
            var Q99;
            {var subQ0=sQuery(id+"F2.wireOp",EDGE,"E48.24");var subQ1=sQuery(id+"F2.wireOp",EDGE,"E48.2");var subQ2=makeQuery(id+"F2.imprint","INTERSECT",VERTEX,{"derivedFrom":[subQ1,subQ0,sQuery(id+"F2.wireOp",EDGE,"E48.25")]});Q99=makeQuery(id+"F2.imprint","IMPRINT",FACE,{"disambiguationData":[TD([[makeQuery(id+"F2.imprint","IMPRINT",EDGE,{"disambiguationData":[TD([[subQ2,-1.0]])],"derivedFrom":subQ1}),1.0]])]});}
            var Q100;
            {var subQ0=sQuery(id+"F2.wireOp",EDGE,"E48.24");var subQ1=sQuery(id+"F2.wireOp",EDGE,"E48.18");var subQ2=makeQuery(id+"F2.imprint","INTERSECT",VERTEX,{"derivedFrom":[sQuery(id+"F2.wireOp",EDGE,"E48.16"),subQ1,subQ0]});Q100=makeQuery(id+"F2.imprint","IMPRINT",FACE,{"disambiguationData":[TD([[makeQuery(id+"F2.imprint","IMPRINT",EDGE,{"disambiguationData":[TD([[subQ2,1.0]])],"derivedFrom":subQ1}),1.0]])]});}
            var Q101;
            {var subQ0=sQuery(id+"F2.wireOp",EDGE,"E48.24");var subQ1=sQuery(id+"F2.wireOp",EDGE,"E48.16");var subQ2=makeQuery(id+"F2.imprint","INTERSECT",VERTEX,{"derivedFrom":[subQ1,sQuery(id+"F2.wireOp",EDGE,"E48.18"),subQ0]});Q101=makeQuery(id+"F2.imprint","IMPRINT",FACE,{"disambiguationData":[TD([[makeQuery(id+"F2.imprint","IMPRINT",EDGE,{"disambiguationData":[TD([[subQ2,-1.0]])],"derivedFrom":subQ1}),1.0]])]});}
            var Q102;
            {var subQ1=sQuery(id+"F2.wireOp",EDGE,"E48.19");var subQ3=sQuery(id+"F2.wireOp",EDGE,"E48.24");var subQ4=makeQuery(id+"F2.imprint","INTERSECT",VERTEX,{"derivedFrom":[subQ1,subQ3]});Q102=makeQuery(id+"F2.imprint","IMPRINT",FACE,{"disambiguationData":[TD([[makeQuery(id+"F2.imprint","IMPRINT",EDGE,{"disambiguationData":[TD([[subQ4,-1.0]])],"derivedFrom":subQ3}),-1.0]])]});}
            var Q103;
            {var subQ1=sQuery(id+"F2.wireOp",EDGE,"E48.19");var subQ3=sQuery(id+"F2.wireOp",EDGE,"E48.24");var subQ4=makeQuery(id+"F2.imprint","INTERSECT",VERTEX,{"derivedFrom":[subQ1,subQ3]});Q103=makeQuery(id+"F2.imprint","IMPRINT",FACE,{"disambiguationData":[TD([[makeQuery(id+"F2.imprint","IMPRINT",EDGE,{"disambiguationData":[TD([[subQ4,1.0]])],"derivedFrom":subQ3}),-1.0]])]});}
            var Q104;
            {var subQ0=sQuery(id+"F2.wireOp",EDGE,"E48.25");var subQ1=sQuery(id+"F2.wireOp",EDGE,"E48.24");var subQ2=makeQuery(id+"F2.imprint","INTERSECT",VERTEX,{"derivedFrom":[subQ1,subQ0,sQuery(id+"F2.wireOp",EDGE,"E48.27")]});Q104=makeQuery(id+"F2.imprint","IMPRINT",FACE,{"disambiguationData":[TD([[makeQuery(id+"F2.imprint","IMPRINT",EDGE,{"disambiguationData":[TD([[subQ2,-1.0]])],"derivedFrom":subQ1}),-1.0]])]});}
            var Q105;
            {var subQ0=sQuery(id+"F2.wireOp",EDGE,"E48.24");var subQ1=sQuery(id+"F2.wireOp",EDGE,"E48.5");var subQ2=makeQuery(id+"F2.imprint","INTERSECT",VERTEX,{"derivedFrom":[subQ1,subQ0,sQuery(id+"F2.wireOp",EDGE,"E48.45")]});Q105=makeQuery(id+"F2.imprint","IMPRINT",FACE,{"disambiguationData":[TD([[makeQuery(id+"F2.imprint","IMPRINT",EDGE,{"disambiguationData":[TD([[subQ2,-1.0]])],"derivedFrom":subQ1}),1.0]])]});}
            var Q106;
            {var subQ0=sQuery(id+"F2.wireOp",EDGE,"E48.24");var subQ1=sQuery(id+"F2.wireOp",EDGE,"E48.21");var subQ2=makeQuery(id+"F2.imprint","INTERSECT",VERTEX,{"derivedFrom":[sQuery(id+"F2.wireOp",EDGE,"E48.10"),subQ1,subQ0]});Q106=makeQuery(id+"F2.imprint","IMPRINT",FACE,{"disambiguationData":[TD([[makeQuery(id+"F2.imprint","IMPRINT",EDGE,{"disambiguationData":[TD([[subQ2,-1.0]])],"derivedFrom":subQ1}),1.0]])]});}
            var Q107;
            {var subQ0=sQuery(id+"F0.wireOp",EDGE,"E40");var subQ1=sQuery(id+"F0.wireOp",EDGE,"E4");var subQ2=makeQuery(id+"F0.imprint","INTERSECT",VERTEX,{"derivedFrom":[sQuery(id+"F0.wireOp",EDGE,"E3"),subQ1,subQ0]});Q107=makeQuery(id+"F0.imprint","IMPRINT",FACE,{"disambiguationData":[TD([[makeQuery(id+"F0.imprint","IMPRINT",EDGE,{"disambiguationData":[TD([[subQ2,-1.0]])],"derivedFrom":subQ1}),1.0]])]});}
            var Q108;
            {var subQ0=sQuery(id+"F2.wireOp",EDGE,"E48.27");var subQ1=sQuery(id+"F2.wireOp",EDGE,"E48.24");var subQ2=makeQuery(id+"F2.imprint","INTERSECT",VERTEX,{"derivedFrom":[subQ1,subQ0,sQuery(id+"F2.wireOp",EDGE,"E48.29")]});Q108=makeQuery(id+"F2.imprint","IMPRINT",FACE,{"disambiguationData":[TD([[makeQuery(id+"F2.imprint","IMPRINT",EDGE,{"disambiguationData":[TD([[subQ2,-1.0]])],"derivedFrom":subQ1}),-1.0]])]});}
            var Q109;
            {var subQ0=sQuery(id+"F2.wireOp",EDGE,"E48.29");var subQ1=sQuery(id+"F2.wireOp",EDGE,"E48.24");var subQ2=makeQuery(id+"F2.imprint","INTERSECT",VERTEX,{"derivedFrom":[subQ1,sQuery(id+"F2.wireOp",EDGE,"E48.27"),subQ0]});Q109=makeQuery(id+"F2.imprint","IMPRINT",FACE,{"disambiguationData":[TD([[makeQuery(id+"F2.imprint","IMPRINT",EDGE,{"disambiguationData":[TD([[subQ2,1.0]])],"derivedFrom":subQ1}),-1.0]])]});}
            var Q110;
            {var subQ0=sQuery(id+"F2.wireOp",EDGE,"E48.24");var subQ1=sQuery(id+"F2.wireOp",EDGE,"E48.10");var subQ2=makeQuery(id+"F2.imprint","INTERSECT",VERTEX,{"derivedFrom":[subQ1,sQuery(id+"F2.wireOp",EDGE,"E48.12"),subQ0]});Q110=makeQuery(id+"F2.imprint","IMPRINT",FACE,{"disambiguationData":[TD([[makeQuery(id+"F2.imprint","IMPRINT",EDGE,{"disambiguationData":[TD([[subQ2,-1.0]])],"derivedFrom":subQ1}),1.0]])]});}
            var Q111;
            {var subQ0=sQuery(id+"F0.wireOp",EDGE,"E40");var subQ1=sQuery(id+"F0.wireOp",EDGE,"E3");var subQ2=makeQuery(id+"F0.imprint","INTERSECT",VERTEX,{"derivedFrom":[subQ1,sQuery(id+"F0.wireOp",EDGE,"E5"),subQ0]});Q111=makeQuery(id+"F0.imprint","IMPRINT",FACE,{"disambiguationData":[TD([[makeQuery(id+"F0.imprint","IMPRINT",EDGE,{"disambiguationData":[TD([[subQ2,-1.0]])],"derivedFrom":subQ1}),1.0]])]});}
            var Q112;
            {var subQ0=sQuery(id+"F2.wireOp",EDGE,"E48.29");var subQ1=sQuery(id+"F2.wireOp",EDGE,"E48.24");var subQ2=makeQuery(id+"F2.imprint","INTERSECT",VERTEX,{"derivedFrom":[subQ1,subQ0,sQuery(id+"F2.wireOp",EDGE,"E48.31")]});Q112=makeQuery(id+"F2.imprint","IMPRINT",FACE,{"disambiguationData":[TD([[makeQuery(id+"F2.imprint","IMPRINT",EDGE,{"disambiguationData":[TD([[subQ2,-1.0]])],"derivedFrom":subQ1}),-1.0]])]});}
            var Q113;
            {var subQ0=sQuery(id+"F2.wireOp",EDGE,"E48.47");var subQ1=sQuery(id+"F2.wireOp",EDGE,"E48.24");var subQ2=makeQuery(id+"F2.imprint","INTERSECT",VERTEX,{"derivedFrom":[subQ1,sQuery(id+"F2.wireOp",EDGE,"E48.32"),subQ0]});Q113=makeQuery(id+"F2.imprint","IMPRINT",FACE,{"disambiguationData":[TD([[makeQuery(id+"F2.imprint","IMPRINT",EDGE,{"disambiguationData":[TD([[subQ2,-1.0]])],"derivedFrom":subQ1}),-1.0]])]});}
            var Q114;
            {var subQ0=sQuery(id+"F2.wireOp",EDGE,"E48.24");var subQ1=sQuery(id+"F2.wireOp",EDGE,"E48.12");var subQ2=makeQuery(id+"F2.imprint","INTERSECT",VERTEX,{"derivedFrom":[subQ1,sQuery(id+"F2.wireOp",EDGE,"E48.14"),subQ0]});Q114=makeQuery(id+"F2.imprint","IMPRINT",FACE,{"disambiguationData":[TD([[makeQuery(id+"F2.imprint","IMPRINT",EDGE,{"disambiguationData":[TD([[subQ2,-1.0]])],"derivedFrom":subQ1}),1.0]])]});}
            var Q115;
            {var subQ0=sQuery(id+"F2.wireOp",EDGE,"E48.24");var subQ1=sQuery(id+"F2.wireOp",EDGE,"E48.14");var subQ2=makeQuery(id+"F2.imprint","INTERSECT",VERTEX,{"derivedFrom":[sQuery(id+"F2.wireOp",EDGE,"E48.12"),subQ1,subQ0]});Q115=makeQuery(id+"F2.imprint","IMPRINT",FACE,{"disambiguationData":[TD([[makeQuery(id+"F2.imprint","IMPRINT",EDGE,{"disambiguationData":[TD([[subQ2,1.0]])],"derivedFrom":subQ1}),1.0]])]});}
            var Q116;
            {var subQ0=sQuery(id+"F2.wireOp",EDGE,"E48.31");var subQ1=sQuery(id+"F2.wireOp",EDGE,"E48.24");var subQ2=makeQuery(id+"F2.imprint","INTERSECT",VERTEX,{"derivedFrom":[sQuery(id+"F2.wireOp",EDGE,"E48.3"),subQ1,subQ0]});Q116=makeQuery(id+"F2.imprint","IMPRINT",FACE,{"disambiguationData":[TD([[makeQuery(id+"F2.imprint","IMPRINT",EDGE,{"disambiguationData":[TD([[subQ2,-1.0]])],"derivedFrom":subQ1}),-1.0]])]});}
            var Q117;
            {var subQ0=sQuery(id+"F2.wireOp",EDGE,"E48.32");var subQ1=sQuery(id+"F2.wireOp",EDGE,"E48.3");var subQ2=makeQuery(id+"F2.imprint","INTERSECT",VERTEX,{"derivedFrom":[subQ1,sQuery(id+"F2.wireOp",EDGE,"E48.20"),subQ0]});Q117=makeQuery(id+"F2.imprint","IMPRINT",FACE,{"disambiguationData":[TD([[makeQuery(id+"F2.imprint","IMPRINT",EDGE,{"disambiguationData":[TD([[subQ2,-1.0]])],"derivedFrom":subQ1}),1.0]])]});}
            var Q118;
            {var subQ0=sQuery(id+"F2.wireOp",EDGE,"E48.24");var subQ1=sQuery(id+"F2.wireOp",EDGE,"E48.14");var subQ2=makeQuery(id+"F2.imprint","INTERSECT",VERTEX,{"derivedFrom":[subQ1,sQuery(id+"F2.wireOp",EDGE,"E48.16"),subQ0]});Q118=makeQuery(id+"F2.imprint","IMPRINT",FACE,{"disambiguationData":[TD([[makeQuery(id+"F2.imprint","IMPRINT",EDGE,{"disambiguationData":[TD([[subQ2,-1.0]])],"derivedFrom":subQ1}),1.0]])]});}
            var Q119;
            {var subQ0=sQuery(id+"F2.wireOp",EDGE,"E48.24");var subQ1=sQuery(id+"F2.wireOp",EDGE,"E48.16");var subQ2=makeQuery(id+"F2.imprint","INTERSECT",VERTEX,{"derivedFrom":[sQuery(id+"F2.wireOp",EDGE,"E48.14"),subQ1,subQ0]});Q119=makeQuery(id+"F2.imprint","IMPRINT",FACE,{"disambiguationData":[TD([[makeQuery(id+"F2.imprint","IMPRINT",EDGE,{"disambiguationData":[TD([[subQ2,1.0]])],"derivedFrom":subQ1}),1.0]])]});}
            var Q120;
            {var subQ0=sQuery(id+"F2.wireOp",EDGE,"E48.24");var subQ1=sQuery(id+"F2.wireOp",EDGE,"E48.3");var subQ2=makeQuery(id+"F2.imprint","INTERSECT",VERTEX,{"derivedFrom":[sQuery(id+"F2.wireOp",EDGE,"E48.2"),subQ1,subQ0]});Q120=makeQuery(id+"F2.imprint","IMPRINT",FACE,{"disambiguationData":[TD([[makeQuery(id+"F2.imprint","IMPRINT",EDGE,{"disambiguationData":[TD([[subQ2,-1.0]])],"derivedFrom":subQ1}),1.0]])]});}
            var Q121;
            {var subQ0=sQuery(id+"F2.wireOp",EDGE,"E48.33");var subQ1=sQuery(id+"F2.wireOp",EDGE,"E48.2");var subQ2=makeQuery(id+"F2.imprint","INTERSECT",VERTEX,{"derivedFrom":[subQ1,sQuery(id+"F2.wireOp",EDGE,"E48.20"),subQ0]});Q121=makeQuery(id+"F2.imprint","IMPRINT",FACE,{"disambiguationData":[TD([[makeQuery(id+"F2.imprint","IMPRINT",EDGE,{"disambiguationData":[TD([[subQ2,-1.0]])],"derivedFrom":subQ1}),1.0]])]});}
            var Q122;
            {var subQ0=sQuery(id+"F0.wireOp",EDGE,"E38");var subQ1=sQuery(id+"F0.wireOp",EDGE,"E20");var subQ2=makeQuery(id+"F0.imprint","INTERSECT",VERTEX,{"derivedFrom":[sQuery(id+"F0.wireOp",EDGE,"E14"),subQ1,subQ0]});Q122=makeQuery(id+"F0.imprint","IMPRINT",FACE,{"disambiguationData":[TD([[makeQuery(id+"F0.imprint","IMPRINT",EDGE,{"disambiguationData":[TD([[subQ2,-1.0]])],"derivedFrom":subQ1}),1.0]])]});}
            var Q123;
            {var subQ0=sQuery(id+"F2.wireOp",EDGE,"E48.34");var subQ1=sQuery(id+"F2.wireOp",EDGE,"E48.20");var subQ2=makeQuery(id+"F2.imprint","INTERSECT",VERTEX,{"derivedFrom":[sQuery(id+"F2.wireOp",EDGE,"E48.16"),subQ1,subQ0]});Q123=makeQuery(id+"F2.imprint","IMPRINT",FACE,{"disambiguationData":[TD([[makeQuery(id+"F2.imprint","IMPRINT",EDGE,{"disambiguationData":[TD([[subQ2,1.0]])],"derivedFrom":subQ1}),-1.0]])]});}
            var Q124;
            {var subQ0=sQuery(id+"F2.wireOp",EDGE,"E48.20");var subQ1=sQuery(id+"F2.wireOp",EDGE,"E48.2");var subQ2=makeQuery(id+"F2.imprint","INTERSECT",VERTEX,{"derivedFrom":[subQ1,subQ0,sQuery(id+"F2.wireOp",EDGE,"E48.41")]});Q124=makeQuery(id+"F2.imprint","IMPRINT",FACE,{"disambiguationData":[TD([[makeQuery(id+"F2.imprint","IMPRINT",EDGE,{"disambiguationData":[TD([[subQ2,-1.0]])],"derivedFrom":subQ1}),1.0]])]});}
            var Q125;
            {var subQ0=sQuery(id+"F2.wireOp",EDGE,"E48.33");var subQ1=sQuery(id+"F2.wireOp",EDGE,"E48.20");var subQ2=makeQuery(id+"F2.imprint","INTERSECT",VERTEX,{"derivedFrom":[sQuery(id+"F2.wireOp",EDGE,"E48.2"),subQ1,subQ0]});Q125=makeQuery(id+"F2.imprint","IMPRINT",FACE,{"disambiguationData":[TD([[makeQuery(id+"F2.imprint","IMPRINT",EDGE,{"disambiguationData":[TD([[subQ2,-1.0]])],"derivedFrom":subQ1}),-1.0]])]});}
            var Q126;
            {var subQ0=sQuery(id+"F2.wireOp",EDGE,"E48.20");var subQ1=sQuery(id+"F2.wireOp",EDGE,"E48.3");var subQ2=makeQuery(id+"F2.imprint","INTERSECT",VERTEX,{"derivedFrom":[subQ1,subQ0,sQuery(id+"F2.wireOp",EDGE,"E48.43")]});Q126=makeQuery(id+"F2.imprint","IMPRINT",FACE,{"disambiguationData":[TD([[makeQuery(id+"F2.imprint","IMPRINT",EDGE,{"disambiguationData":[TD([[subQ2,-1.0]])],"derivedFrom":subQ1}),1.0]])]});}
            var Q127;
            {var subQ0=sQuery(id+"F2.wireOp",EDGE,"E48.33");var subQ1=sQuery(id+"F2.wireOp",EDGE,"E48.20");var subQ2=makeQuery(id+"F2.imprint","INTERSECT",VERTEX,{"derivedFrom":[sQuery(id+"F2.wireOp",EDGE,"E48.14"),subQ1,subQ0]});Q127=makeQuery(id+"F2.imprint","IMPRINT",FACE,{"disambiguationData":[TD([[makeQuery(id+"F2.imprint","IMPRINT",EDGE,{"disambiguationData":[TD([[subQ2,1.0]])],"derivedFrom":subQ1}),-1.0]])]});}
            var Q128;
            {var subQ0=sQuery(id+"F2.wireOp",EDGE,"E48.14");var subQ1=sQuery(id+"F2.wireOp",EDGE,"E48.3");var subQ2=makeQuery(id+"F2.imprint","INTERSECT",VERTEX,{"derivedFrom":[subQ1,sQuery(id+"F2.wireOp",EDGE,"E48.13"),subQ0]});Q128=makeQuery(id+"F2.imprint","IMPRINT",FACE,{"disambiguationData":[TD([[makeQuery(id+"F2.imprint","IMPRINT",EDGE,{"disambiguationData":[TD([[subQ2,-1.0]])],"derivedFrom":subQ1}),1.0]])]});}
            var Q129;
            {var subQ0=sQuery(id+"F2.wireOp",EDGE,"E48.32");var subQ1=sQuery(id+"F2.wireOp",EDGE,"E48.20");var subQ2=makeQuery(id+"F2.imprint","INTERSECT",VERTEX,{"derivedFrom":[sQuery(id+"F2.wireOp",EDGE,"E48.3"),subQ1,subQ0]});Q129=makeQuery(id+"F2.imprint","IMPRINT",FACE,{"disambiguationData":[TD([[makeQuery(id+"F2.imprint","IMPRINT",EDGE,{"disambiguationData":[TD([[subQ2,-1.0]])],"derivedFrom":subQ1}),-1.0]])]});}
            var Q130;
            {var subQ0=sQuery(id+"F2.wireOp",EDGE,"E48.31");var subQ1=sQuery(id+"F2.wireOp",EDGE,"E48.14");var subQ2=makeQuery(id+"F2.imprint","INTERSECT",VERTEX,{"derivedFrom":[sQuery(id+"F2.wireOp",EDGE,"E48.13"),subQ1,subQ0]});Q130=makeQuery(id+"F2.imprint","IMPRINT",FACE,{"disambiguationData":[TD([[makeQuery(id+"F2.imprint","IMPRINT",EDGE,{"disambiguationData":[TD([[subQ2,-1.0]])],"derivedFrom":subQ1}),1.0]])]});}
            var Q131;
            {var subQ0=sQuery(id+"F2.wireOp",EDGE,"E48.32");var subQ1=sQuery(id+"F2.wireOp",EDGE,"E48.20");var subQ2=makeQuery(id+"F2.imprint","INTERSECT",VERTEX,{"derivedFrom":[sQuery(id+"F2.wireOp",EDGE,"E48.12"),subQ1,subQ0]});Q131=makeQuery(id+"F2.imprint","IMPRINT",FACE,{"disambiguationData":[TD([[makeQuery(id+"F2.imprint","IMPRINT",EDGE,{"disambiguationData":[TD([[subQ2,1.0]])],"derivedFrom":subQ1}),-1.0]])]});}
            var Q132;
            {var subQ0=sQuery(id+"F2.wireOp",EDGE,"E48.20");var subQ1=sQuery(id+"F2.wireOp",EDGE,"E48.12");var subQ2=makeQuery(id+"F2.imprint","INTERSECT",VERTEX,{"derivedFrom":[subQ1,subQ0,sQuery(id+"F2.wireOp",EDGE,"E48.32")]});Q132=makeQuery(id+"F2.imprint","IMPRINT",FACE,{"disambiguationData":[TD([[makeQuery(id+"F2.imprint","IMPRINT",EDGE,{"disambiguationData":[TD([[subQ2,-1.0]])],"derivedFrom":subQ1}),1.0]])]});}
            var Q133;
            {var subQ0=sQuery(id+"F0.wireOp",EDGE,"E11");var subQ1=sQuery(id+"F0.wireOp",EDGE,"E5");var subQ2=makeQuery(id+"F0.imprint","INTERSECT",VERTEX,{"derivedFrom":[subQ1,subQ0,sQuery(id+"F0.wireOp",EDGE,"E34")]});Q133=makeQuery(id+"F0.imprint","IMPRINT",FACE,{"disambiguationData":[TD([[makeQuery(id+"F0.imprint","IMPRINT",EDGE,{"disambiguationData":[TD([[subQ2,-1.0]])],"derivedFrom":subQ1}),1.0]])]});}
            var Q134;
            {var subQ0=sQuery(id+"F0.wireOp",EDGE,"E38");var subQ1=sQuery(id+"F0.wireOp",EDGE,"E18");var subQ2=makeQuery(id+"F0.imprint","INTERSECT",VERTEX,{"derivedFrom":[sQuery(id+"F0.wireOp",EDGE,"E3"),subQ1,subQ0]});Q134=makeQuery(id+"F0.imprint","IMPRINT",FACE,{"disambiguationData":[TD([[makeQuery(id+"F0.imprint","IMPRINT",EDGE,{"disambiguationData":[TD([[subQ2,1.0]])],"derivedFrom":subQ1}),1.0]])]});}
            var Q135;
            {var subQ0=sQuery(id+"F0.wireOp",EDGE,"E38");var subQ1=sQuery(id+"F0.wireOp",EDGE,"E3");var subQ2=makeQuery(id+"F0.imprint","INTERSECT",VERTEX,{"derivedFrom":[subQ1,sQuery(id+"F0.wireOp",EDGE,"E18"),subQ0]});Q135=makeQuery(id+"F0.imprint","IMPRINT",FACE,{"disambiguationData":[TD([[makeQuery(id+"F0.imprint","IMPRINT",EDGE,{"disambiguationData":[TD([[subQ2,-1.0]])],"derivedFrom":subQ1}),1.0]])]});}
            var Q136;
            {var subQ0=sQuery(id+"F2.wireOp",EDGE,"E48.20");var subQ1=sQuery(id+"F2.wireOp",EDGE,"E48.10");var subQ2=makeQuery(id+"F2.imprint","INTERSECT",VERTEX,{"derivedFrom":[subQ1,subQ0,sQuery(id+"F2.wireOp",EDGE,"E48.47")]});Q136=makeQuery(id+"F2.imprint","IMPRINT",FACE,{"disambiguationData":[TD([[makeQuery(id+"F2.imprint","IMPRINT",EDGE,{"disambiguationData":[TD([[subQ2,-1.0]])],"derivedFrom":subQ1}),1.0]])]});}
            var Q137;
            {var subQ0=sQuery(id+"F2.wireOp",EDGE,"E48.38");var subQ1=sQuery(id+"F2.wireOp",EDGE,"E48.20");var subQ2=makeQuery(id+"F2.imprint","INTERSECT",VERTEX,{"derivedFrom":[subQ1,sQuery(id+"F2.wireOp",EDGE,"E48.27"),subQ0]});Q137=makeQuery(id+"F2.imprint","IMPRINT",FACE,{"disambiguationData":[TD([[makeQuery(id+"F2.imprint","IMPRINT",EDGE,{"disambiguationData":[TD([[subQ2,1.0]])],"derivedFrom":subQ1}),-1.0]])]});}
            var Q138;
            {var subQ0=sQuery(id+"F2.wireOp",EDGE,"E48.27");var subQ1=sQuery(id+"F2.wireOp",EDGE,"E48.10");var subQ2=makeQuery(id+"F2.imprint","INTERSECT",VERTEX,{"derivedFrom":[subQ1,sQuery(id+"F2.wireOp",EDGE,"E48.13"),subQ0]});Q138=makeQuery(id+"F2.imprint","IMPRINT",FACE,{"disambiguationData":[TD([[makeQuery(id+"F2.imprint","IMPRINT",EDGE,{"disambiguationData":[TD([[subQ2,-1.0]])],"derivedFrom":subQ1}),1.0]])]});}
            var Q139;
            {var subQ0=sQuery(id+"F2.wireOp",EDGE,"E48.39");var subQ1=sQuery(id+"F2.wireOp",EDGE,"E48.20");var subQ2=makeQuery(id+"F2.imprint","INTERSECT",VERTEX,{"derivedFrom":[sQuery(id+"F2.wireOp",EDGE,"E48.10"),subQ1,subQ0]});Q139=makeQuery(id+"F2.imprint","IMPRINT",FACE,{"disambiguationData":[TD([[makeQuery(id+"F2.imprint","IMPRINT",EDGE,{"disambiguationData":[TD([[subQ2,-1.0]])],"derivedFrom":subQ1}),-1.0]])]});}
            var Q140;
            {var subQ0=sQuery(id+"F2.wireOp",EDGE,"E48.27");var subQ1=sQuery(id+"F2.wireOp",EDGE,"E48.20");var subQ2=makeQuery(id+"F2.imprint","INTERSECT",VERTEX,{"derivedFrom":[sQuery(id+"F2.wireOp",EDGE,"E48.5"),subQ1,subQ0]});Q140=makeQuery(id+"F2.imprint","IMPRINT",FACE,{"disambiguationData":[TD([[makeQuery(id+"F2.imprint","IMPRINT",EDGE,{"disambiguationData":[TD([[subQ2,1.0]])],"derivedFrom":subQ1}),-1.0]])]});}
            var Q141;
            {var subQ0=sQuery(id+"F2.wireOp",EDGE,"E48.20");var subQ1=sQuery(id+"F2.wireOp",EDGE,"E48.5");var subQ2=makeQuery(id+"F2.imprint","INTERSECT",VERTEX,{"derivedFrom":[subQ1,subQ0,sQuery(id+"F2.wireOp",EDGE,"E48.27")]});Q141=makeQuery(id+"F2.imprint","IMPRINT",FACE,{"disambiguationData":[TD([[makeQuery(id+"F2.imprint","IMPRINT",EDGE,{"disambiguationData":[TD([[subQ2,-1.0]])],"derivedFrom":subQ1}),1.0]])]});}
            var Q142;
            {var subQ0=sQuery(id+"F2.wireOp",EDGE,"E48.21");var subQ3=sQuery(id+"F2.wireOp",EDGE,"E48.25");var subQ5=makeQuery(id+"F2.imprint","INTERSECT",VERTEX,{"derivedFrom":[sQuery(id+"F2.wireOp",EDGE,"E48.13"),subQ0,subQ3]});Q142=makeQuery(id+"F2.imprint","IMPRINT",FACE,{"disambiguationData":[TD([[makeQuery(id+"F2.imprint","IMPRINT",EDGE,{"disambiguationData":[TD([[subQ5,1.0]])],"derivedFrom":subQ3}),1.0]])]});}
            var Q143;
            {var subQ0=sQuery(id+"F2.wireOp",EDGE,"E48.41");var subQ1=sQuery(id+"F2.wireOp",EDGE,"E48.5");var subQ2=makeQuery(id+"F2.imprint","INTERSECT",VERTEX,{"derivedFrom":[subQ1,sQuery(id+"F2.wireOp",EDGE,"E48.13"),subQ0]});Q143=makeQuery(id+"F2.imprint","IMPRINT",FACE,{"disambiguationData":[TD([[makeQuery(id+"F2.imprint","IMPRINT",EDGE,{"disambiguationData":[TD([[subQ2,-1.0]])],"derivedFrom":subQ1}),1.0]])]});}
            var Q144;
            {var subQ0=sQuery(id+"F2.wireOp",EDGE,"E48.20");var subQ1=sQuery(id+"F2.wireOp",EDGE,"E48.18");var subQ2=makeQuery(id+"F2.imprint","INTERSECT",VERTEX,{"derivedFrom":[sQuery(id+"F2.wireOp",EDGE,"E48.5"),subQ1,subQ0]});Q144=makeQuery(id+"F2.imprint","IMPRINT",FACE,{"disambiguationData":[TD([[makeQuery(id+"F2.imprint","IMPRINT",EDGE,{"disambiguationData":[TD([[subQ2,-1.0]])],"derivedFrom":subQ1}),1.0]])]});}
            var Q145;
            {var subQ0=sQuery(id+"F0.wireOp",EDGE,"E14");var subQ1=sQuery(id+"F0.wireOp",EDGE,"E6");var subQ2=makeQuery(id+"F0.imprint","INTERSECT",VERTEX,{"derivedFrom":[subQ1,subQ0,sQuery(id+"F0.wireOp",EDGE,"E34")]});Q145=makeQuery(id+"F0.imprint","IMPRINT",FACE,{"disambiguationData":[TD([[makeQuery(id+"F0.imprint","IMPRINT",EDGE,{"disambiguationData":[TD([[subQ2,-1.0]])],"derivedFrom":subQ1}),1.0]])]});}
            var Q146;
            {var subQ0=sQuery(id+"F2.wireOp",EDGE,"E48.18");var subQ3=sQuery(id+"F2.wireOp",EDGE,"E48.41");var subQ5=makeQuery(id+"F2.imprint","INTERSECT",VERTEX,{"derivedFrom":[subQ0,subQ3]});Q146=makeQuery(id+"F2.imprint","IMPRINT",FACE,{"disambiguationData":[TD([[makeQuery(id+"F2.imprint","IMPRINT",EDGE,{"disambiguationData":[TD([[subQ5,1.0]])],"derivedFrom":subQ0}),1.0]])]});}
            var Q147;
            {var subQ0=sQuery(id+"F2.wireOp",EDGE,"E48.41");var subQ3=sQuery(id+"F2.wireOp",EDGE,"E48.25");var subQ5=makeQuery(id+"F2.imprint","INTERSECT",VERTEX,{"derivedFrom":[subQ3,subQ0]});Q147=makeQuery(id+"F2.imprint","IMPRINT",FACE,{"disambiguationData":[TD([[makeQuery(id+"F2.imprint","IMPRINT",EDGE,{"disambiguationData":[TD([[subQ5,-1.0]])],"derivedFrom":subQ3}),1.0]])]});}
            var Q148;
            {var subQ0=sQuery(id+"F0.wireOp",EDGE,"E21");var subQ1=sQuery(id+"F0.wireOp",EDGE,"E14");var subQ2=makeQuery(id+"F0.imprint","INTERSECT",VERTEX,{"derivedFrom":[subQ1,subQ0]});Q148=makeQuery(id+"F0.imprint","IMPRINT",FACE,{"disambiguationData":[TD([[makeQuery(id+"F0.imprint","IMPRINT",EDGE,{"disambiguationData":[TD([[subQ2,1.0]])],"derivedFrom":subQ1}),1.0]])]});}
            var Q149;
            {var subQ0=sQuery(id+"F2.wireOp",EDGE,"E48.34");var subQ1=sQuery(id+"F2.wireOp",EDGE,"E48.2");var subQ2=makeQuery(id+"F2.imprint","INTERSECT",VERTEX,{"derivedFrom":[subQ1,subQ0]});Q149=makeQuery(id+"F2.imprint","IMPRINT",FACE,{"disambiguationData":[TD([[makeQuery(id+"F2.imprint","IMPRINT",EDGE,{"disambiguationData":[TD([[subQ2,1.0]])],"derivedFrom":subQ1}),1.0]])]});}
            var Q150;
            {var subQ0=sQuery(id+"F0.wireOp",EDGE,"E24");var subQ1=sQuery(id+"F0.wireOp",EDGE,"E15");var subQ2=makeQuery(id+"F0.imprint","INTERSECT",VERTEX,{"derivedFrom":[subQ1,subQ0]});Q150=makeQuery(id+"F0.imprint","IMPRINT",FACE,{"disambiguationData":[TD([[makeQuery(id+"F0.imprint","IMPRINT",EDGE,{"disambiguationData":[TD([[subQ2,-1.0]])],"derivedFrom":subQ1}),1.0]])]});}
            var Q151;
            {var subQ0=sQuery(id+"F2.wireOp",EDGE,"E48.21");var subQ1=sQuery(id+"F2.wireOp",EDGE,"E48.5");var subQ2=makeQuery(id+"F2.imprint","INTERSECT",VERTEX,{"derivedFrom":[subQ1,subQ0]});Q151=makeQuery(id+"F2.imprint","IMPRINT",FACE,{"disambiguationData":[TD([[makeQuery(id+"F2.imprint","IMPRINT",EDGE,{"disambiguationData":[TD([[subQ2,1.0]])],"derivedFrom":subQ1}),1.0]])]});}
            var Q152;
            {var subQ0=sQuery(id+"F2.wireOp",EDGE,"E48.39");var subQ3=sQuery(id+"F2.wireOp",EDGE,"E48.21");var subQ5=makeQuery(id+"F2.imprint","INTERSECT",VERTEX,{"derivedFrom":[subQ3,subQ0]});Q152=makeQuery(id+"F2.imprint","IMPRINT",FACE,{"disambiguationData":[TD([[makeQuery(id+"F2.imprint","IMPRINT",EDGE,{"disambiguationData":[TD([[subQ5,1.0]])],"derivedFrom":subQ3}),1.0]])]});}
            var Q153;
            {var subQ0=sQuery(id+"F2.wireOp",EDGE,"E48.39");var subQ3=sQuery(id+"F2.wireOp",EDGE,"E48.27");var subQ5=makeQuery(id+"F2.imprint","INTERSECT",VERTEX,{"derivedFrom":[subQ3,subQ0]});Q153=makeQuery(id+"F2.imprint","IMPRINT",FACE,{"disambiguationData":[TD([[makeQuery(id+"F2.imprint","IMPRINT",EDGE,{"disambiguationData":[TD([[subQ5,-1.0]])],"derivedFrom":subQ3}),1.0]])]});}
            var Q154;
            {var subQ0=sQuery(id+"F2.wireOp",EDGE,"E48.27");var subQ3=sQuery(id+"F2.wireOp",EDGE,"E48.45");var subQ5=makeQuery(id+"F2.imprint","INTERSECT",VERTEX,{"derivedFrom":[subQ0,subQ3]});Q154=makeQuery(id+"F2.imprint","IMPRINT",FACE,{"disambiguationData":[TD([[makeQuery(id+"F2.imprint","IMPRINT",EDGE,{"disambiguationData":[TD([[subQ5,1.0]])],"derivedFrom":subQ0}),1.0]])]});}
            var Q155;
            {var subQ0=sQuery(id+"F2.wireOp",EDGE,"E48.45");var subQ1=sQuery(id+"F2.wireOp",EDGE,"E48.10");var subQ2=makeQuery(id+"F2.imprint","INTERSECT",VERTEX,{"derivedFrom":[subQ1,subQ0]});Q155=makeQuery(id+"F2.imprint","IMPRINT",FACE,{"disambiguationData":[TD([[makeQuery(id+"F2.imprint","IMPRINT",EDGE,{"disambiguationData":[TD([[subQ2,-1.0]])],"derivedFrom":subQ1}),1.0]])]});}
            var Q156;
            {var subQ0=sQuery(id+"F0.wireOp",EDGE,"E17");var subQ1=sQuery(id+"F0.wireOp",EDGE,"E3");var subQ2=makeQuery(id+"F0.imprint","INTERSECT",VERTEX,{"derivedFrom":[subQ1,subQ0]});Q156=makeQuery(id+"F0.imprint","IMPRINT",FACE,{"disambiguationData":[TD([[makeQuery(id+"F0.imprint","IMPRINT",EDGE,{"disambiguationData":[TD([[subQ2,-1.0]])],"derivedFrom":subQ1}),1.0]])]});}
            var Q157;
            {var subQ0=sQuery(id+"F0.wireOp",EDGE,"E26");var subQ1=sQuery(id+"F0.wireOp",EDGE,"E3");var subQ2=makeQuery(id+"F0.imprint","INTERSECT",VERTEX,{"derivedFrom":[subQ1,subQ0]});Q157=makeQuery(id+"F0.imprint","IMPRINT",FACE,{"disambiguationData":[TD([[makeQuery(id+"F0.imprint","IMPRINT",EDGE,{"disambiguationData":[TD([[subQ2,1.0]])],"derivedFrom":subQ1}),1.0]])]});}
            var Q158;
            {var subQ0=sQuery(id+"F2.wireOp",EDGE,"E48.29");var subQ3=sQuery(id+"F2.wireOp",EDGE,"E48.47");var subQ5=makeQuery(id+"F2.imprint","INTERSECT",VERTEX,{"derivedFrom":[subQ0,subQ3]});Q158=makeQuery(id+"F2.imprint","IMPRINT",FACE,{"disambiguationData":[TD([[makeQuery(id+"F2.imprint","IMPRINT",EDGE,{"disambiguationData":[TD([[subQ5,1.0]])],"derivedFrom":subQ0}),1.0]])]});}
            var Q159;
            {var subQ0=sQuery(id+"F2.wireOp",EDGE,"E48.47");var subQ1=sQuery(id+"F2.wireOp",EDGE,"E48.12");var subQ2=makeQuery(id+"F2.imprint","INTERSECT",VERTEX,{"derivedFrom":[subQ1,subQ0]});Q159=makeQuery(id+"F2.imprint","IMPRINT",FACE,{"disambiguationData":[TD([[makeQuery(id+"F2.imprint","IMPRINT",EDGE,{"disambiguationData":[TD([[subQ2,-1.0]])],"derivedFrom":subQ1}),1.0]])]});}
            var Q160;
            {var subQ0=sQuery(id+"F0.wireOp",EDGE,"E18");var subQ1=sQuery(id+"F0.wireOp",EDGE,"E5");var subQ2=makeQuery(id+"F0.imprint","INTERSECT",VERTEX,{"derivedFrom":[subQ1,subQ0]});Q160=makeQuery(id+"F0.imprint","IMPRINT",FACE,{"disambiguationData":[TD([[makeQuery(id+"F0.imprint","IMPRINT",EDGE,{"disambiguationData":[TD([[subQ2,-1.0]])],"derivedFrom":subQ1}),1.0]])]});}
            var Q161;
            {var subQ0=sQuery(id+"F2.wireOp",EDGE,"E48.31");var subQ3=sQuery(id+"F2.wireOp",EDGE,"E48.40");var subQ5=makeQuery(id+"F2.imprint","INTERSECT",VERTEX,{"derivedFrom":[subQ0,subQ3]});Q161=makeQuery(id+"F2.imprint","IMPRINT",FACE,{"disambiguationData":[TD([[makeQuery(id+"F2.imprint","IMPRINT",EDGE,{"disambiguationData":[TD([[subQ5,-1.0]])],"derivedFrom":subQ0}),1.0]])]});}
            var Q162;
            {var subQ0=sQuery(id+"F2.wireOp",EDGE,"E48.31");var subQ3=sQuery(id+"F2.wireOp",EDGE,"E48.32");var subQ5=makeQuery(id+"F2.imprint","INTERSECT",VERTEX,{"derivedFrom":[subQ0,subQ3]});Q162=makeQuery(id+"F2.imprint","IMPRINT",FACE,{"disambiguationData":[TD([[makeQuery(id+"F2.imprint","IMPRINT",EDGE,{"disambiguationData":[TD([[subQ5,1.0]])],"derivedFrom":subQ0}),1.0]])]});}
            var Q163;
            {var subQ0=sQuery(id+"F2.wireOp",EDGE,"E48.32");var subQ3=sQuery(id+"F2.wireOp",EDGE,"E48.14");var subQ5=makeQuery(id+"F2.imprint","INTERSECT",VERTEX,{"derivedFrom":[subQ3,subQ0]});Q163=makeQuery(id+"F2.imprint","IMPRINT",FACE,{"disambiguationData":[TD([[makeQuery(id+"F2.imprint","IMPRINT",EDGE,{"disambiguationData":[TD([[subQ5,-1.0]])],"derivedFrom":subQ3}),1.0]])]});}
            var Q164;
            {var subQ0=sQuery(id+"F2.wireOp",EDGE,"E48.14");var subQ3=sQuery(id+"F2.wireOp",EDGE,"E48.42");var subQ5=makeQuery(id+"F2.imprint","INTERSECT",VERTEX,{"derivedFrom":[subQ0,subQ3]});Q164=makeQuery(id+"F2.imprint","IMPRINT",FACE,{"disambiguationData":[TD([[makeQuery(id+"F2.imprint","IMPRINT",EDGE,{"disambiguationData":[TD([[subQ5,1.0]])],"derivedFrom":subQ0}),1.0]])]});}
            var Q165;
            {var subQ0=sQuery(id+"F2.wireOp",EDGE,"E48.42");var subQ1=sQuery(id+"F2.wireOp",EDGE,"E48.3");var subQ2=makeQuery(id+"F2.imprint","INTERSECT",VERTEX,{"derivedFrom":[subQ1,subQ0]});Q165=makeQuery(id+"F2.imprint","IMPRINT",FACE,{"disambiguationData":[TD([[makeQuery(id+"F2.imprint","IMPRINT",EDGE,{"disambiguationData":[TD([[subQ2,-1.0]])],"derivedFrom":subQ1}),1.0]])]});}
            var Q166;
            {var subQ0=sQuery(id+"F0.wireOp",EDGE,"E28");var subQ1=sQuery(id+"F0.wireOp",EDGE,"E13");var subQ2=makeQuery(id+"F0.imprint","INTERSECT",VERTEX,{"derivedFrom":[subQ1,subQ0]});Q166=makeQuery(id+"F0.imprint","IMPRINT",FACE,{"disambiguationData":[TD([[makeQuery(id+"F0.imprint","IMPRINT",EDGE,{"disambiguationData":[TD([[subQ2,-1.0]])],"derivedFrom":subQ1}),1.0]])]});}
            var Q167;
            {var subQ0=sQuery(id+"F0.wireOp",EDGE,"E20");var subQ1=sQuery(id+"F0.wireOp",EDGE,"E13");var subQ2=makeQuery(id+"F0.imprint","INTERSECT",VERTEX,{"derivedFrom":[subQ1,subQ0]});Q167=makeQuery(id+"F0.imprint","IMPRINT",FACE,{"disambiguationData":[TD([[makeQuery(id+"F0.imprint","IMPRINT",EDGE,{"disambiguationData":[TD([[subQ2,1.0]])],"derivedFrom":subQ1}),1.0]])]});}
            var Q168;
            {var subQ0=sQuery(id+"F0.wireOp",EDGE,"E20");var subQ1=sQuery(id+"F0.wireOp",EDGE,"E8");var subQ2=makeQuery(id+"F0.imprint","INTERSECT",VERTEX,{"derivedFrom":[subQ1,subQ0]});Q168=makeQuery(id+"F0.imprint","IMPRINT",FACE,{"disambiguationData":[TD([[makeQuery(id+"F0.imprint","IMPRINT",EDGE,{"disambiguationData":[TD([[subQ2,-1.0]])],"derivedFrom":subQ1}),1.0]])]});}
            var Q169;
            {var subQ0=sQuery(id+"F2.wireOp",EDGE,"E48.43");var subQ1=sQuery(id+"F2.wireOp",EDGE,"E48.2");var subQ2=makeQuery(id+"F2.imprint","INTERSECT",VERTEX,{"derivedFrom":[subQ1,subQ0]});Q169=makeQuery(id+"F2.imprint","IMPRINT",FACE,{"disambiguationData":[TD([[makeQuery(id+"F2.imprint","IMPRINT",EDGE,{"disambiguationData":[TD([[subQ2,-1.0]])],"derivedFrom":subQ1}),1.0]])]});}
            var Q170;
            {var subQ0=sQuery(id+"F0.wireOp",EDGE,"E14");var subQ1=sQuery(id+"F0.wireOp",EDGE,"E6");var subQ2=makeQuery(id+"F0.imprint","INTERSECT",VERTEX,{"derivedFrom":[subQ1,subQ0,sQuery(id+"F0.wireOp",EDGE,"E34")]});Q170=makeQuery(id+"F0.imprint","IMPRINT",FACE,{"disambiguationData":[TD([[makeQuery(id+"F0.imprint","IMPRINT",EDGE,{"disambiguationData":[TD([[subQ2,-1.0]])],"derivedFrom":subQ1}),1.0]])]});}
            var Q171;
            {var subQ0=sQuery(id+"F2.wireOp",EDGE,"E48.20");var subQ1=sQuery(id+"F2.wireOp",EDGE,"E48.18");var subQ2=makeQuery(id+"F2.imprint","INTERSECT",VERTEX,{"derivedFrom":[sQuery(id+"F2.wireOp",EDGE,"E48.5"),subQ1,subQ0]});Q171=makeQuery(id+"F2.imprint","IMPRINT",FACE,{"disambiguationData":[TD([[makeQuery(id+"F2.imprint","IMPRINT",EDGE,{"disambiguationData":[TD([[subQ2,-1.0]])],"derivedFrom":subQ1}),1.0]])]});}
            var Q172;
            {var subQ0=sQuery(id+"F2.wireOp",EDGE,"E48.41");var subQ1=sQuery(id+"F2.wireOp",EDGE,"E48.5");var subQ2=makeQuery(id+"F2.imprint","INTERSECT",VERTEX,{"derivedFrom":[subQ1,sQuery(id+"F2.wireOp",EDGE,"E48.13"),subQ0]});Q172=makeQuery(id+"F2.imprint","IMPRINT",FACE,{"disambiguationData":[TD([[makeQuery(id+"F2.imprint","IMPRINT",EDGE,{"disambiguationData":[TD([[subQ2,-1.0]])],"derivedFrom":subQ1}),1.0]])]});}
            var Q173;
            {var subQ0=sQuery(id+"F2.wireOp",EDGE,"E48.21");var subQ3=sQuery(id+"F2.wireOp",EDGE,"E48.25");var subQ5=makeQuery(id+"F2.imprint","INTERSECT",VERTEX,{"derivedFrom":[sQuery(id+"F2.wireOp",EDGE,"E48.13"),subQ0,subQ3]});Q173=makeQuery(id+"F2.imprint","IMPRINT",FACE,{"disambiguationData":[TD([[makeQuery(id+"F2.imprint","IMPRINT",EDGE,{"disambiguationData":[TD([[subQ5,1.0]])],"derivedFrom":subQ3}),1.0]])]});}
            var Q174;
            {var subQ0=sQuery(id+"F2.wireOp",EDGE,"E48.27");var subQ1=sQuery(id+"F2.wireOp",EDGE,"E48.20");var subQ2=makeQuery(id+"F2.imprint","INTERSECT",VERTEX,{"derivedFrom":[sQuery(id+"F2.wireOp",EDGE,"E48.5"),subQ1,subQ0]});Q174=makeQuery(id+"F2.imprint","IMPRINT",FACE,{"disambiguationData":[TD([[makeQuery(id+"F2.imprint","IMPRINT",EDGE,{"disambiguationData":[TD([[subQ2,1.0]])],"derivedFrom":subQ1}),-1.0]])]});}
            var Q175;
            {var subQ0=sQuery(id+"F2.wireOp",EDGE,"E48.39");var subQ1=sQuery(id+"F2.wireOp",EDGE,"E48.20");var subQ2=makeQuery(id+"F2.imprint","INTERSECT",VERTEX,{"derivedFrom":[sQuery(id+"F2.wireOp",EDGE,"E48.10"),subQ1,subQ0]});Q175=makeQuery(id+"F2.imprint","IMPRINT",FACE,{"disambiguationData":[TD([[makeQuery(id+"F2.imprint","IMPRINT",EDGE,{"disambiguationData":[TD([[subQ2,-1.0]])],"derivedFrom":subQ1}),-1.0]])]});}
            var Q176;
            {var subQ0=sQuery(id+"F2.wireOp",EDGE,"E48.27");var subQ1=sQuery(id+"F2.wireOp",EDGE,"E48.10");var subQ2=makeQuery(id+"F2.imprint","INTERSECT",VERTEX,{"derivedFrom":[subQ1,sQuery(id+"F2.wireOp",EDGE,"E48.13"),subQ0]});Q176=makeQuery(id+"F2.imprint","IMPRINT",FACE,{"disambiguationData":[TD([[makeQuery(id+"F2.imprint","IMPRINT",EDGE,{"disambiguationData":[TD([[subQ2,-1.0]])],"derivedFrom":subQ1}),1.0]])]});}
            var Q177;
            {var subQ0=sQuery(id+"F2.wireOp",EDGE,"E48.47");var subQ1=sQuery(id+"F2.wireOp",EDGE,"E48.12");var subQ2=makeQuery(id+"F2.imprint","INTERSECT",VERTEX,{"derivedFrom":[subQ1,subQ0]});Q177=makeQuery(id+"F2.imprint","IMPRINT",FACE,{"disambiguationData":[TD([[makeQuery(id+"F2.imprint","IMPRINT",EDGE,{"disambiguationData":[TD([[subQ2,-1.0]])],"derivedFrom":subQ1}),1.0]])]});}
            var Q178;
            {var subQ0=sQuery(id+"F2.wireOp",EDGE,"E48.29");var subQ3=sQuery(id+"F2.wireOp",EDGE,"E48.47");var subQ5=makeQuery(id+"F2.imprint","INTERSECT",VERTEX,{"derivedFrom":[subQ0,subQ3]});Q178=makeQuery(id+"F2.imprint","IMPRINT",FACE,{"disambiguationData":[TD([[makeQuery(id+"F2.imprint","IMPRINT",EDGE,{"disambiguationData":[TD([[subQ5,1.0]])],"derivedFrom":subQ0}),1.0]])]});}
            var Q179;
            {var subQ0=sQuery(id+"F0.wireOp",EDGE,"E26");var subQ1=sQuery(id+"F0.wireOp",EDGE,"E3");var subQ2=makeQuery(id+"F0.imprint","INTERSECT",VERTEX,{"derivedFrom":[subQ1,subQ0]});Q179=makeQuery(id+"F0.imprint","IMPRINT",FACE,{"disambiguationData":[TD([[makeQuery(id+"F0.imprint","IMPRINT",EDGE,{"disambiguationData":[TD([[subQ2,1.0]])],"derivedFrom":subQ1}),1.0]])]});}
            var Q180;
            {var subQ0=sQuery(id+"F0.wireOp",EDGE,"E18");var subQ1=sQuery(id+"F0.wireOp",EDGE,"E5");var subQ2=makeQuery(id+"F0.imprint","INTERSECT",VERTEX,{"derivedFrom":[subQ1,subQ0]});Q180=makeQuery(id+"F0.imprint","IMPRINT",FACE,{"disambiguationData":[TD([[makeQuery(id+"F0.imprint","IMPRINT",EDGE,{"disambiguationData":[TD([[subQ2,-1.0]])],"derivedFrom":subQ1}),1.0]])]});}
            var Q181;
            {var subQ0=sQuery(id+"F0.wireOp",EDGE,"E17");var subQ1=sQuery(id+"F0.wireOp",EDGE,"E3");var subQ2=makeQuery(id+"F0.imprint","INTERSECT",VERTEX,{"derivedFrom":[subQ1,subQ0]});Q181=makeQuery(id+"F0.imprint","IMPRINT",FACE,{"disambiguationData":[TD([[makeQuery(id+"F0.imprint","IMPRINT",EDGE,{"disambiguationData":[TD([[subQ2,-1.0]])],"derivedFrom":subQ1}),1.0]])]});}
            var Q182;
            {var subQ0=sQuery(id+"F2.wireOp",EDGE,"E48.45");var subQ1=sQuery(id+"F2.wireOp",EDGE,"E48.10");var subQ2=makeQuery(id+"F2.imprint","INTERSECT",VERTEX,{"derivedFrom":[subQ1,subQ0]});Q182=makeQuery(id+"F2.imprint","IMPRINT",FACE,{"disambiguationData":[TD([[makeQuery(id+"F2.imprint","IMPRINT",EDGE,{"disambiguationData":[TD([[subQ2,-1.0]])],"derivedFrom":subQ1}),1.0]])]});}
            var Q183;
            {var subQ0=sQuery(id+"F2.wireOp",EDGE,"E48.27");var subQ3=sQuery(id+"F2.wireOp",EDGE,"E48.45");var subQ5=makeQuery(id+"F2.imprint","INTERSECT",VERTEX,{"derivedFrom":[subQ0,subQ3]});Q183=makeQuery(id+"F2.imprint","IMPRINT",FACE,{"disambiguationData":[TD([[makeQuery(id+"F2.imprint","IMPRINT",EDGE,{"disambiguationData":[TD([[subQ5,1.0]])],"derivedFrom":subQ0}),1.0]])]});}
            var Q184;
            {var subQ0=sQuery(id+"F2.wireOp",EDGE,"E48.39");var subQ3=sQuery(id+"F2.wireOp",EDGE,"E48.27");var subQ5=makeQuery(id+"F2.imprint","INTERSECT",VERTEX,{"derivedFrom":[subQ3,subQ0]});Q184=makeQuery(id+"F2.imprint","IMPRINT",FACE,{"disambiguationData":[TD([[makeQuery(id+"F2.imprint","IMPRINT",EDGE,{"disambiguationData":[TD([[subQ5,-1.0]])],"derivedFrom":subQ3}),1.0]])]});}
            var Q185;
            {var subQ0=sQuery(id+"F2.wireOp",EDGE,"E48.39");var subQ3=sQuery(id+"F2.wireOp",EDGE,"E48.21");var subQ5=makeQuery(id+"F2.imprint","INTERSECT",VERTEX,{"derivedFrom":[subQ3,subQ0]});Q185=makeQuery(id+"F2.imprint","IMPRINT",FACE,{"disambiguationData":[TD([[makeQuery(id+"F2.imprint","IMPRINT",EDGE,{"disambiguationData":[TD([[subQ5,1.0]])],"derivedFrom":subQ3}),1.0]])]});}
            var Q186;
            {var subQ0=sQuery(id+"F2.wireOp",EDGE,"E48.21");var subQ1=sQuery(id+"F2.wireOp",EDGE,"E48.5");var subQ2=makeQuery(id+"F2.imprint","INTERSECT",VERTEX,{"derivedFrom":[subQ1,subQ0]});Q186=makeQuery(id+"F2.imprint","IMPRINT",FACE,{"disambiguationData":[TD([[makeQuery(id+"F2.imprint","IMPRINT",EDGE,{"disambiguationData":[TD([[subQ2,1.0]])],"derivedFrom":subQ1}),1.0]])]});}
            var Q187;
            {var subQ0=sQuery(id+"F0.wireOp",EDGE,"E24");var subQ1=sQuery(id+"F0.wireOp",EDGE,"E15");var subQ2=makeQuery(id+"F0.imprint","INTERSECT",VERTEX,{"derivedFrom":[subQ1,subQ0]});Q187=makeQuery(id+"F0.imprint","IMPRINT",FACE,{"disambiguationData":[TD([[makeQuery(id+"F0.imprint","IMPRINT",EDGE,{"disambiguationData":[TD([[subQ2,-1.0]])],"derivedFrom":subQ1}),1.0]])]});}
            var Q188;
            {var subQ0=sQuery(id+"F2.wireOp",EDGE,"E48.41");var subQ3=sQuery(id+"F2.wireOp",EDGE,"E48.25");var subQ5=makeQuery(id+"F2.imprint","INTERSECT",VERTEX,{"derivedFrom":[subQ3,subQ0]});Q188=makeQuery(id+"F2.imprint","IMPRINT",FACE,{"disambiguationData":[TD([[makeQuery(id+"F2.imprint","IMPRINT",EDGE,{"disambiguationData":[TD([[subQ5,-1.0]])],"derivedFrom":subQ3}),1.0]])]});}
            var Q189;
            {var subQ0=sQuery(id+"F2.wireOp",EDGE,"E48.18");var subQ3=sQuery(id+"F2.wireOp",EDGE,"E48.41");var subQ5=makeQuery(id+"F2.imprint","INTERSECT",VERTEX,{"derivedFrom":[subQ0,subQ3]});Q189=makeQuery(id+"F2.imprint","IMPRINT",FACE,{"disambiguationData":[TD([[makeQuery(id+"F2.imprint","IMPRINT",EDGE,{"disambiguationData":[TD([[subQ5,1.0]])],"derivedFrom":subQ0}),1.0]])]});}
            var Q190;
            {var subQ0=sQuery(id+"F0.wireOp",EDGE,"E21");var subQ1=sQuery(id+"F0.wireOp",EDGE,"E14");var subQ2=makeQuery(id+"F0.imprint","INTERSECT",VERTEX,{"derivedFrom":[subQ1,subQ0]});Q190=makeQuery(id+"F0.imprint","IMPRINT",FACE,{"disambiguationData":[TD([[makeQuery(id+"F0.imprint","IMPRINT",EDGE,{"disambiguationData":[TD([[subQ2,1.0]])],"derivedFrom":subQ1}),1.0]])]});}
            var Q191;
            {var subQ0=sQuery(id+"F2.wireOp",EDGE,"E48.34");var subQ1=sQuery(id+"F2.wireOp",EDGE,"E48.2");var subQ2=makeQuery(id+"F2.imprint","INTERSECT",VERTEX,{"derivedFrom":[subQ1,subQ0]});Q191=makeQuery(id+"F2.imprint","IMPRINT",FACE,{"disambiguationData":[TD([[makeQuery(id+"F2.imprint","IMPRINT",EDGE,{"disambiguationData":[TD([[subQ2,1.0]])],"derivedFrom":subQ1}),1.0]])]});}
            var Q192;
            {var subQ0=sQuery(id+"F2.wireOp",EDGE,"E48.43");var subQ1=sQuery(id+"F2.wireOp",EDGE,"E48.2");var subQ2=makeQuery(id+"F2.imprint","INTERSECT",VERTEX,{"derivedFrom":[subQ1,subQ0]});Q192=makeQuery(id+"F2.imprint","IMPRINT",FACE,{"disambiguationData":[TD([[makeQuery(id+"F2.imprint","IMPRINT",EDGE,{"disambiguationData":[TD([[subQ2,-1.0]])],"derivedFrom":subQ1}),1.0]])]});}
            extrude(context, id + "F4", {"entities" : qUnion([Q0, Q1, Q2, Q3, Q4, Q5, Q6, Q7, Q8, Q9, Q10, Q11, Q12, Q13, Q14, Q15, Q16, Q17, Q18, Q19, Q20, Q21, Q22, Q23, Q24, Q25, Q26, Q27, Q28, Q29, Q30, Q31, Q32, Q33, Q34, Q35, Q36, Q37, Q38, Q39, Q40, Q41, Q42, Q43, Q44, Q45, Q46, Q47, Q48, Q49, Q50, Q51, Q52, Q53, Q54, Q55, Q56, Q57, Q58, Q59, Q60, Q61, Q62, Q63, Q64, Q65, Q66, Q67, Q68, Q69, Q70, Q71, Q72, Q73, Q74, Q75, Q76, Q77, Q78, Q79, Q80, Q81, Q82, Q83, Q84, Q85, Q86, Q87, Q88, Q89, Q90, Q91, Q92, Q93, Q94, Q95, Q96, Q97, Q98, Q99, Q100, Q101, Q102, Q103, Q104, Q105, Q106, Q107, Q108, Q109, Q110, Q111, Q112, Q113, Q114, Q115, Q116, Q117, Q118, Q119, Q120, Q121, Q122, Q123, Q124, Q125, Q126, Q127, Q128, Q129, Q130, Q131, Q132, Q133, Q134, Q135, Q136, Q137, Q138, Q139, Q140, Q141, Q142, Q143, Q144, Q145, Q146, Q147, Q148, Q149, Q150, Q151, Q152, Q153, Q154, Q155, Q156, Q157, Q158, Q159, Q160, Q161, Q162, Q163, Q164, Q165, Q166, Q167, Q168, Q169, Q170, Q171, Q172, Q173, Q174, Q175, Q176, Q177, Q178, Q179, Q180, Q181, Q182, Q183, Q184, Q185, Q186, Q187, Q188, Q189, Q190, Q191, Q192]), "depth" : 12 * mm, "hasDraft" : true, "draftAngle" : 6 * degree, "draftPullDirection" : true});
        }
    });
